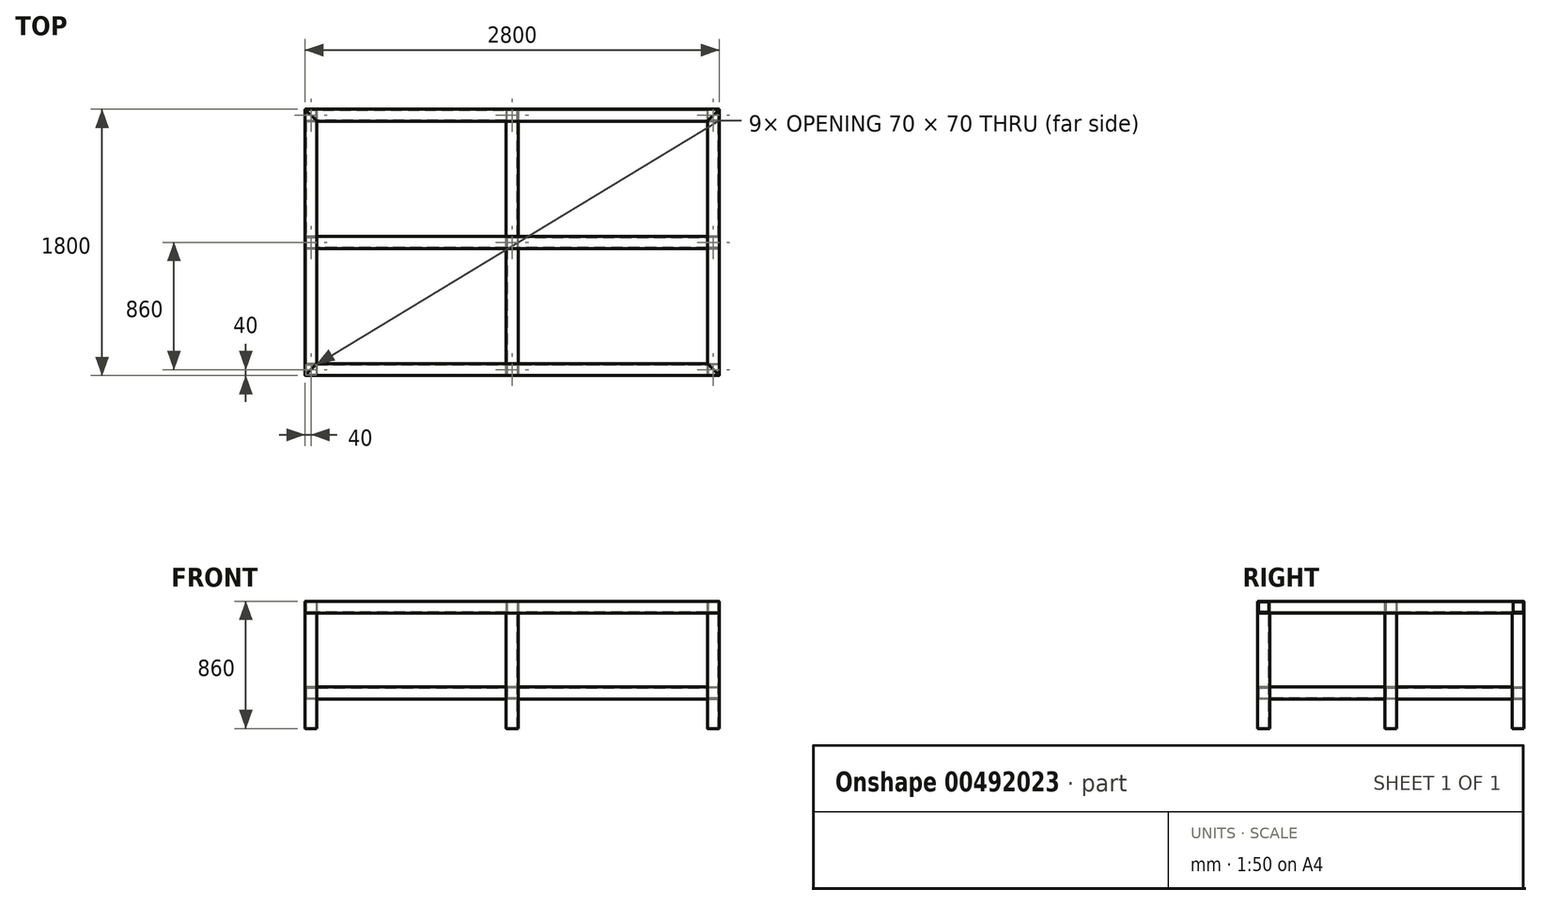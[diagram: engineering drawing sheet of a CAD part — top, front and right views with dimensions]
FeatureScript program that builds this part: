
annotation { "Feature Type Name" : "Feature", "Feature Type Description" : "" }
export const myFeature = defineFeature(function(context is Context, id is Id, definition is map)
    precondition{}
    {
        {
            var Q0;
            Q0=qCreatedBy(makeId("Top.planeOp"),FACE);
            var sketch = newSketch(context, id + "F0", { "sketchPlane" : qUnion([Q0])});
            skLineSegment(sketch, "E0", {"start": v(-1400, -900) * mm, "end": v(-1400, 900) * mm});
            skLineSegment(sketch, "E1", {"start": v(-1400, 900) * mm, "end": v(-1320, 820) * mm});
            skLineSegment(sketch, "E2", {"start": v(-1320, 820) * mm, "end": v(-1320, -820) * mm});
            skLineSegment(sketch, "E3", {"start": v(-1320, -820) * mm, "end": v(-1400, -900) * mm});
            skLineSegment(sketch, "E4.MirrorCS", {"start": v(1320, -820) * mm, "end": v(1400, -900) * mm});
            skLineSegment(sketch, "E5.MirrorCS", {"start": v(1400, 900) * mm, "end": v(1320, 820) * mm});
            skLineSegment(sketch, "E6.MirrorCS", {"start": v(1320, 820) * mm, "end": v(1320, -820) * mm});
            skLineSegment(sketch, "E7.MirrorCS", {"start": v(1400, -900) * mm, "end": v(1400, 900) * mm});
            skSolve(sketch);
        }
        {
            var Q0;
            Q0=makeQuery(id+"F0.imprint","IMPRINT",FACE,{"disambiguationData":[TD([[makeQuery(id+"F0.imprint","IMPRINT",EDGE,{"derivedFrom":sQuery(id+"F0.wireOp",EDGE,"E0")}),-1.0]])]});
            var Q1;
            Q1=makeQuery(id+"F0.imprint","IMPRINT",FACE,{"disambiguationData":[TD([[makeQuery(id+"F0.imprint","IMPRINT",EDGE,{"derivedFrom":sQuery(id+"F0.wireOp",EDGE,"E4.MirrorCS")}),1.0]])]});
            extrude(context, id + "F1", {"entities" : qUnion([Q0, Q1]), "depth" : 80 * mm});
        }
        {
            var Q0;
            Q0=qCreatedBy(makeId("Front.planeOp"),FACE);
            var sketch = newSketch(context, id + "F2", { "sketchPlane" : qUnion([Q0])});
            skLineSegment(sketch, "E8.bottom", {"start": v(-1395, 75) * mm, "end": v(-1325, 75) * mm});
            skLineSegment(sketch, "E8.top", {"start": v(-1395, 5) * mm, "end": v(-1325, 5) * mm});
            skLineSegment(sketch, "E8.left", {"start": v(-1395, 75) * mm, "end": v(-1395, 5) * mm});
            skLineSegment(sketch, "E8.right", {"start": v(-1325, 75) * mm, "end": v(-1325, 5) * mm});
            skLineSegment(sketch, "E9.MirrorCS", {"start": v(1325, 75) * mm, "end": v(1325, 5) * mm});
            skLineSegment(sketch, "E10.MirrorCS", {"start": v(1395, 75) * mm, "end": v(1395, 5) * mm});
            skLineSegment(sketch, "E11.MirrorCS", {"start": v(1395, 75) * mm, "end": v(1325, 75) * mm});
            skLineSegment(sketch, "E12.MirrorCS", {"start": v(1395, 5) * mm, "end": v(1325, 5) * mm});
            skSolve(sketch);
        }
        {
            var Q0;
            Q0 = qSketchRegion(id + "F2", true);
            extrude(context, id + "F3", {"entities" : qUnion([Q0]), "operationType" : NewBodyOperationType.REMOVE, "endBound" : BoundingType.SYMMETRIC, "oppositeDirection" : true, "depth" : 2000 * mm});
        }
        {
            var Q0;
            Q0=makeQuery(id+"F1.opExtrude","CAP_EDGE",EDGE,{"disambiguationData":[OSD([sQuery(id+"F0.wireOp",EDGE,"E0")])],"isStart":false});
            var Q1;
            Q1=makeQuery(id+"F1.opExtrude","CAP_EDGE",EDGE,{"disambiguationData":[OSD([sQuery(id+"F0.wireOp",EDGE,"E2")])],"isStart":false});
            var Q2;
            Q2=makeQuery(id+"F1.opExtrude","CAP_EDGE",EDGE,{"disambiguationData":[OSD([sQuery(id+"F0.wireOp",EDGE,"E2")])],"isStart":true});
            var Q3;
            Q3=makeQuery(id+"F1.opExtrude","CAP_EDGE",EDGE,{"disambiguationData":[OSD([sQuery(id+"F0.wireOp",EDGE,"E0")])],"isStart":true});
            var Q4;
            Q4=makeQuery(id+"F3.boolean.opBoolean","COPY",EDGE,{"derivedFrom":makeQuery(id+"F3.opExtrude","SWEPT_EDGE",EDGE,{"disambiguationData":[OSD([sQuery(id+"F2.wireOp",EDGE,"E8.bottom"),sQuery(id+"F2.wireOp",EDGE,"E8.right")])]})});
            var Q5;
            Q5=makeQuery(id+"F3.boolean.opBoolean","COPY",EDGE,{"derivedFrom":makeQuery(id+"F3.opExtrude","SWEPT_EDGE",EDGE,{"disambiguationData":[OSD([sQuery(id+"F2.wireOp",EDGE,"E8.bottom"),sQuery(id+"F2.wireOp",EDGE,"E8.left")])]})});
            var Q6;
            Q6=makeQuery(id+"F3.boolean.opBoolean","COPY",EDGE,{"derivedFrom":makeQuery(id+"F3.opExtrude","SWEPT_EDGE",EDGE,{"disambiguationData":[OSD([sQuery(id+"F2.wireOp",EDGE,"E8.top"),sQuery(id+"F2.wireOp",EDGE,"E8.right")])]})});
            var Q7;
            Q7=makeQuery(id+"F3.boolean.opBoolean","COPY",EDGE,{"derivedFrom":makeQuery(id+"F3.opExtrude","SWEPT_EDGE",EDGE,{"disambiguationData":[OSD([sQuery(id+"F2.wireOp",EDGE,"E8.top"),sQuery(id+"F2.wireOp",EDGE,"E8.left")])]})});
            fillet(context, id + "F4", {"entities" : qUnion([Q0, Q1, Q2, Q3, Q4, Q5, Q6, Q7]), "radius" : 4 * mm, "tangentPropagation" : true, "allowEdgeOverflow" : false});
        }
        {
            var Q0;
            Q0=makeQuery(id+"F1.opExtrude","CAP_EDGE",EDGE,{"disambiguationData":[OSD([sQuery(id+"F0.wireOp",EDGE,"E7.MirrorCS")])],"isStart":false});
            var Q1;
            Q1=makeQuery(id+"F1.opExtrude","CAP_EDGE",EDGE,{"disambiguationData":[OSD([sQuery(id+"F0.wireOp",EDGE,"E7.MirrorCS")])],"isStart":true});
            var Q2;
            Q2=makeQuery(id+"F1.opExtrude","CAP_EDGE",EDGE,{"disambiguationData":[OSD([sQuery(id+"F0.wireOp",EDGE,"E6.MirrorCS")])],"isStart":false});
            var Q3;
            Q3=makeQuery(id+"F1.opExtrude","CAP_EDGE",EDGE,{"disambiguationData":[OSD([sQuery(id+"F0.wireOp",EDGE,"E6.MirrorCS")])],"isStart":true});
            var Q4;
            Q4=makeQuery(id+"F3.boolean.opBoolean","COPY",EDGE,{"derivedFrom":makeQuery(id+"F3.opExtrude","SWEPT_EDGE",EDGE,{"disambiguationData":[OSD([sQuery(id+"F2.wireOp",EDGE,"E10.MirrorCS"),sQuery(id+"F2.wireOp",EDGE,"E11.MirrorCS")])]})});
            var Q5;
            Q5=makeQuery(id+"F3.boolean.opBoolean","COPY",EDGE,{"derivedFrom":makeQuery(id+"F3.opExtrude","SWEPT_EDGE",EDGE,{"disambiguationData":[OSD([sQuery(id+"F2.wireOp",EDGE,"E10.MirrorCS"),sQuery(id+"F2.wireOp",EDGE,"E12.MirrorCS")])]})});
            var Q6;
            Q6=makeQuery(id+"F3.boolean.opBoolean","COPY",EDGE,{"derivedFrom":makeQuery(id+"F3.opExtrude","SWEPT_EDGE",EDGE,{"disambiguationData":[OSD([sQuery(id+"F2.wireOp",EDGE,"E9.MirrorCS"),sQuery(id+"F2.wireOp",EDGE,"E12.MirrorCS")])]})});
            var Q7;
            Q7=makeQuery(id+"F3.boolean.opBoolean","COPY",EDGE,{"derivedFrom":makeQuery(id+"F3.opExtrude","SWEPT_EDGE",EDGE,{"disambiguationData":[OSD([sQuery(id+"F2.wireOp",EDGE,"E9.MirrorCS"),sQuery(id+"F2.wireOp",EDGE,"E11.MirrorCS")])]})});
            fillet(context, id + "F5", {"entities" : qUnion([Q0, Q1, Q2, Q3, Q4, Q5, Q6, Q7]), "radius" : 4 * mm, "tangentPropagation" : true, "allowEdgeOverflow" : false});
        }
        {
            var Q0;
            Q0=qCreatedBy(makeId("Top.planeOp"),FACE);
            var sketch = newSketch(context, id + "F6", { "sketchPlane" : qUnion([Q0])});
            skLineSegment(sketch, "E13", {"start": v(-1400, 900) * mm, "end": v(1400, 900) * mm});
            skLineSegment(sketch, "E14", {"start": v(1400, 900) * mm, "end": v(1320, 820) * mm});
            skLineSegment(sketch, "E15", {"start": v(1320, 820) * mm, "end": v(-1320, 820) * mm});
            skLineSegment(sketch, "E16", {"start": v(-1320, 820) * mm, "end": v(-1400, 900) * mm});
            skLineSegment(sketch, "E17.MirrorCS", {"start": v(-1320, -820) * mm, "end": v(-1400, -900) * mm});
            skLineSegment(sketch, "E18.MirrorCS", {"start": v(1400, -900) * mm, "end": v(1320, -820) * mm});
            skLineSegment(sketch, "E19.MirrorCS", {"start": v(1320, -820) * mm, "end": v(-1320, -820) * mm});
            skLineSegment(sketch, "E20.MirrorCS", {"start": v(-1400, -900) * mm, "end": v(1400, -900) * mm});
            skSolve(sketch);
        }
        {
            var Q0;
            Q0=makeQuery(id+"F6.imprint","IMPRINT",FACE,{"disambiguationData":[TD([[makeQuery(id+"F6.imprint","IMPRINT",EDGE,{"derivedFrom":sQuery(id+"F6.wireOp",EDGE,"E17.MirrorCS")}),1.0]])]});
            var Q1;
            Q1=makeQuery(id+"F6.imprint","IMPRINT",FACE,{"disambiguationData":[TD([[makeQuery(id+"F6.imprint","IMPRINT",EDGE,{"derivedFrom":sQuery(id+"F6.wireOp",EDGE,"E13")}),-1.0]])]});
            extrude(context, id + "F7", {"entities" : qUnion([Q0, Q1]), "depth" : 80 * mm});
        }
        {
            var Q0;
            Q0=qCreatedBy(makeId("Right.planeOp"),FACE);
            var sketch = newSketch(context, id + "F8", { "sketchPlane" : qUnion([Q0])});
            skLineSegment(sketch, "E21.bottom", {"start": v(-895, 75) * mm, "end": v(-825, 75) * mm});
            skLineSegment(sketch, "E21.top", {"start": v(-895, 5) * mm, "end": v(-825, 5) * mm});
            skLineSegment(sketch, "E21.left", {"start": v(-895, 75) * mm, "end": v(-895, 5) * mm});
            skLineSegment(sketch, "E21.right", {"start": v(-825, 75) * mm, "end": v(-825, 5) * mm});
            skLineSegment(sketch, "E22.MirrorCS", {"start": v(895, 75) * mm, "end": v(895, 5) * mm});
            skLineSegment(sketch, "E23.MirrorCS", {"start": v(895, 75) * mm, "end": v(825, 75) * mm});
            skLineSegment(sketch, "E24.MirrorCS", {"start": v(825, 75) * mm, "end": v(825, 5) * mm});
            skLineSegment(sketch, "E25.MirrorCS", {"start": v(895, 5) * mm, "end": v(825, 5) * mm});
            skSolve(sketch);
        }
        {
            var Q0;
            Q0 = qSketchRegion(id + "F8", true);
            extrude(context, id + "F9", {"entities" : qUnion([Q0]), "operationType" : NewBodyOperationType.REMOVE, "endBound" : BoundingType.SYMMETRIC, "oppositeDirection" : true, "depth" : 2800 * mm});
        }
        {
            var Q0;
            Q0=makeQuery(id+"F7.opExtrude","CAP_EDGE",EDGE,{"disambiguationData":[OSD([sQuery(id+"F6.wireOp",EDGE,"E20.MirrorCS")])],"isStart":true});
            var Q1;
            Q1=makeQuery(id+"F7.opExtrude","CAP_EDGE",EDGE,{"disambiguationData":[OSD([sQuery(id+"F6.wireOp",EDGE,"E19.MirrorCS")])],"isStart":true});
            var Q2;
            Q2=makeQuery(id+"F7.opExtrude","CAP_EDGE",EDGE,{"disambiguationData":[OSD([sQuery(id+"F6.wireOp",EDGE,"E19.MirrorCS")])],"isStart":false});
            var Q3;
            Q3=makeQuery(id+"F7.opExtrude","CAP_EDGE",EDGE,{"disambiguationData":[OSD([sQuery(id+"F6.wireOp",EDGE,"E20.MirrorCS")])],"isStart":false});
            var Q4;
            Q4=makeQuery(id+"F9.boolean.opBoolean","COPY",EDGE,{"derivedFrom":makeQuery(id+"F9.opExtrude","SWEPT_EDGE",EDGE,{"disambiguationData":[OSD([sQuery(id+"F8.wireOp",EDGE,"E21.top"),sQuery(id+"F8.wireOp",EDGE,"E21.left")])]})});
            var Q5;
            Q5=makeQuery(id+"F9.boolean.opBoolean","COPY",EDGE,{"derivedFrom":makeQuery(id+"F9.opExtrude","SWEPT_EDGE",EDGE,{"disambiguationData":[OSD([sQuery(id+"F8.wireOp",EDGE,"E21.top"),sQuery(id+"F8.wireOp",EDGE,"E21.right")])]})});
            var Q6;
            Q6=makeQuery(id+"F9.boolean.opBoolean","COPY",EDGE,{"derivedFrom":makeQuery(id+"F9.opExtrude","SWEPT_EDGE",EDGE,{"disambiguationData":[OSD([sQuery(id+"F8.wireOp",EDGE,"E21.bottom"),sQuery(id+"F8.wireOp",EDGE,"E21.right")])]})});
            var Q7;
            Q7=makeQuery(id+"F9.boolean.opBoolean","COPY",EDGE,{"derivedFrom":makeQuery(id+"F9.opExtrude","SWEPT_EDGE",EDGE,{"disambiguationData":[OSD([sQuery(id+"F8.wireOp",EDGE,"E21.bottom"),sQuery(id+"F8.wireOp",EDGE,"E21.left")])]})});
            fillet(context, id + "F10", {"entities" : qUnion([Q0, Q1, Q2, Q3, Q4, Q5, Q6, Q7]), "radius" : 4 * mm, "tangentPropagation" : true, "allowEdgeOverflow" : false});
        }
        {
            var Q0;
            Q0=makeQuery(id+"F7.opExtrude","CAP_EDGE",EDGE,{"disambiguationData":[OSD([sQuery(id+"F6.wireOp",EDGE,"E15")])],"isStart":false});
            var Q1;
            Q1=makeQuery(id+"F7.opExtrude","CAP_EDGE",EDGE,{"disambiguationData":[OSD([sQuery(id+"F6.wireOp",EDGE,"E13")])],"isStart":false});
            var Q2;
            Q2=makeQuery(id+"F7.opExtrude","CAP_EDGE",EDGE,{"disambiguationData":[OSD([sQuery(id+"F6.wireOp",EDGE,"E15")])],"isStart":true});
            var Q3;
            Q3=makeQuery(id+"F9.boolean.opBoolean","COPY",EDGE,{"derivedFrom":makeQuery(id+"F9.opExtrude","SWEPT_EDGE",EDGE,{"disambiguationData":[OSD([sQuery(id+"F8.wireOp",EDGE,"E22.MirrorCS"),sQuery(id+"F8.wireOp",EDGE,"E25.MirrorCS")])]})});
            var Q4;
            Q4=makeQuery(id+"F9.boolean.opBoolean","COPY",EDGE,{"derivedFrom":makeQuery(id+"F9.opExtrude","SWEPT_EDGE",EDGE,{"disambiguationData":[OSD([sQuery(id+"F8.wireOp",EDGE,"E22.MirrorCS"),sQuery(id+"F8.wireOp",EDGE,"E23.MirrorCS")])]})});
            var Q5;
            Q5=makeQuery(id+"F7.opExtrude","CAP_EDGE",EDGE,{"disambiguationData":[OSD([sQuery(id+"F6.wireOp",EDGE,"E13")])],"isStart":true});
            var Q6;
            Q6=makeQuery(id+"F9.boolean.opBoolean","COPY",EDGE,{"derivedFrom":makeQuery(id+"F9.opExtrude","SWEPT_EDGE",EDGE,{"disambiguationData":[OSD([sQuery(id+"F8.wireOp",EDGE,"E23.MirrorCS"),sQuery(id+"F8.wireOp",EDGE,"E24.MirrorCS")])]})});
            var Q7;
            Q7=makeQuery(id+"F9.boolean.opBoolean","COPY",EDGE,{"derivedFrom":makeQuery(id+"F9.opExtrude","SWEPT_EDGE",EDGE,{"disambiguationData":[OSD([sQuery(id+"F8.wireOp",EDGE,"E24.MirrorCS"),sQuery(id+"F8.wireOp",EDGE,"E25.MirrorCS")])]})});
            fillet(context, id + "F11", {"entities" : qUnion([Q0, Q1, Q2, Q3, Q4, Q5, Q6, Q7]), "radius" : 4 * mm, "tangentPropagation" : true, "allowEdgeOverflow" : false});
        }
        {
            var Q0;
            Q0=qCreatedBy(makeId("Top.planeOp"),FACE);
            var sketch = newSketch(context, id + "F12", { "sketchPlane" : qUnion([Q0])});
            skLineSegment(sketch, "E26.bottom", {"start": v(-1320, 40) * mm, "end": v(1320, 40) * mm});
            skLineSegment(sketch, "E26.top", {"start": v(-1320, -40) * mm, "end": v(1320, -40) * mm});
            skLineSegment(sketch, "E26.left", {"start": v(-1320, 40) * mm, "end": v(-1320, -40) * mm});
            skLineSegment(sketch, "E26.right", {"start": v(1320, 40) * mm, "end": v(1320, -40) * mm});
            skSolve(sketch);
        }
        {
            var Q0;
            Q0=makeQuery(id+"F12.imprint","IMPRINT",FACE,{"disambiguationData":[TD([[makeQuery(id+"F12.imprint","IMPRINT",EDGE,{"derivedFrom":sQuery(id+"F12.wireOp",EDGE,"E26.bottom")}),-1.0]])]});
            extrude(context, id + "F13", {"entities" : qUnion([Q0]), "depth" : 80 * mm});
        }
        {
            var Q0;
            Q0=makeQuery(id+"F13.opExtrude","SWEPT_FACE",FACE,{"disambiguationData":[OSD([sQuery(id+"F12.wireOp",EDGE,"E26.left")])]});
            var sketch = newSketch(context, id + "F14", { "sketchPlane" : qUnion([Q0])});
            skLineSegment(sketch, "E27.bottom", {"start": v(-35, 5) * mm, "end": v(35, 5) * mm});
            skLineSegment(sketch, "E27.top", {"start": v(-35, 75) * mm, "end": v(35, 75) * mm});
            skLineSegment(sketch, "E27.left", {"start": v(-35, 5) * mm, "end": v(-35, 75) * mm});
            skLineSegment(sketch, "E27.right", {"start": v(35, 5) * mm, "end": v(35, 75) * mm});
            skSolve(sketch);
        }
        {
            var Q0;
            Q0 = qSketchRegion(id + "F14", true);
            extrude(context, id + "F15", {"entities" : qUnion([Q0]), "operationType" : NewBodyOperationType.REMOVE, "oppositeDirection" : true, "depth" : 2640 * mm});
        }
        {
            var Q0;
            Q0=makeQuery(id+"F13.opExtrude","CAP_EDGE",EDGE,{"disambiguationData":[OSD([sQuery(id+"F12.wireOp",EDGE,"E26.top")])],"isStart":true});
            var Q1;
            Q1=makeQuery(id+"F13.opExtrude","CAP_EDGE",EDGE,{"disambiguationData":[OSD([sQuery(id+"F12.wireOp",EDGE,"E26.bottom")])],"isStart":true});
            var Q2;
            Q2=makeQuery(id+"F13.opExtrude","CAP_EDGE",EDGE,{"disambiguationData":[OSD([sQuery(id+"F12.wireOp",EDGE,"E26.bottom")])],"isStart":false});
            var Q3;
            Q3=makeQuery(id+"F15.boolean.opBoolean","COPY",EDGE,{"derivedFrom":makeQuery(id+"F15.opExtrude","SWEPT_EDGE",EDGE,{"disambiguationData":[OSD([sQuery(id+"F14.wireOp",EDGE,"E27.top"),sQuery(id+"F14.wireOp",EDGE,"E27.right")])]})});
            var Q4;
            Q4=makeQuery(id+"F13.opExtrude","CAP_EDGE",EDGE,{"disambiguationData":[OSD([sQuery(id+"F12.wireOp",EDGE,"E26.top")])],"isStart":false});
            var Q5;
            Q5=makeQuery(id+"F15.boolean.opBoolean","COPY",EDGE,{"derivedFrom":makeQuery(id+"F15.opExtrude","SWEPT_EDGE",EDGE,{"disambiguationData":[OSD([sQuery(id+"F14.wireOp",EDGE,"E27.bottom"),sQuery(id+"F14.wireOp",EDGE,"E27.right")])]})});
            var Q6;
            Q6=makeQuery(id+"F15.boolean.opBoolean","COPY",EDGE,{"derivedFrom":makeQuery(id+"F15.opExtrude","SWEPT_EDGE",EDGE,{"disambiguationData":[OSD([sQuery(id+"F14.wireOp",EDGE,"E27.bottom"),sQuery(id+"F14.wireOp",EDGE,"E27.left")])]})});
            var Q7;
            Q7=makeQuery(id+"F15.boolean.opBoolean","COPY",EDGE,{"derivedFrom":makeQuery(id+"F15.opExtrude","SWEPT_EDGE",EDGE,{"disambiguationData":[OSD([sQuery(id+"F14.wireOp",EDGE,"E27.top"),sQuery(id+"F14.wireOp",EDGE,"E27.left")])]})});
            fillet(context, id + "F16", {"entities" : qUnion([Q0, Q1, Q2, Q3, Q4, Q5, Q6, Q7]), "radius" : 5 * mm, "tangentPropagation" : true, "allowEdgeOverflow" : false});
        }
        {
            var Q0;
            Q0=qCreatedBy(makeId("Top.planeOp"),FACE);
            var sketch = newSketch(context, id + "F17", { "sketchPlane" : qUnion([Q0])});
            skLineSegment(sketch, "E28.bottom", {"start": v(-40, 820) * mm, "end": v(40, 820) * mm});
            skLineSegment(sketch, "E28.top", {"start": v(-40, 40) * mm, "end": v(40, 40) * mm});
            skLineSegment(sketch, "E28.left", {"start": v(-40, 820) * mm, "end": v(-40, 40) * mm});
            skLineSegment(sketch, "E28.right", {"start": v(40, 820) * mm, "end": v(40, 40) * mm});
            skLineSegment(sketch, "E29.bottom", {"start": v(-40, -40) * mm, "end": v(40, -40) * mm});
            skLineSegment(sketch, "E29.top", {"start": v(-40, -820) * mm, "end": v(40, -820) * mm});
            skLineSegment(sketch, "E29.left", {"start": v(-40, -40) * mm, "end": v(-40, -820) * mm});
            skLineSegment(sketch, "E29.right", {"start": v(40, -40) * mm, "end": v(40, -820) * mm});
            skSolve(sketch);
        }
        {
            var Q0;
            Q0 = qSketchRegion(id + "F17", true);
            extrude(context, id + "F18", {"entities" : qUnion([Q0]), "depth" : 80 * mm});
        }
        {
            var Q0;
            Q0=makeQuery(id+"F18.opExtrude","SWEPT_FACE",FACE,{"disambiguationData":[OSD([sQuery(id+"F17.wireOp",EDGE,"E29.top")])]});
            var sketch = newSketch(context, id + "F19", { "sketchPlane" : qUnion([Q0])});
            skLineSegment(sketch, "E30.bottom", {"start": v(-35, 75) * mm, "end": v(35, 75) * mm});
            skLineSegment(sketch, "E30.top", {"start": v(-35, 5) * mm, "end": v(35, 5) * mm});
            skLineSegment(sketch, "E30.left", {"start": v(-35, 75) * mm, "end": v(-35, 5) * mm});
            skLineSegment(sketch, "E30.right", {"start": v(35, 75) * mm, "end": v(35, 5) * mm});
            skSolve(sketch);
        }
        {
            var Q0;
            Q0 = qSketchRegion(id + "F19", true);
            extrude(context, id + "F20", {"entities" : qUnion([Q0]), "operationType" : NewBodyOperationType.REMOVE, "oppositeDirection" : true, "depth" : 1560 * mm});
        }
        {
            var Q0;
            Q0=makeQuery(id+"F18.opExtrude","SWEPT_FACE",FACE,{"disambiguationData":[OSD([sQuery(id+"F17.wireOp",EDGE,"E28.bottom")])]});
            var sketch = newSketch(context, id + "F21", { "sketchPlane" : qUnion([Q0])});
            skLineSegment(sketch, "E31.bottom", {"start": v(35, 75) * mm, "end": v(-35, 75) * mm});
            skLineSegment(sketch, "E31.top", {"start": v(35, 5) * mm, "end": v(-35, 5) * mm});
            skLineSegment(sketch, "E31.left", {"start": v(35, 75) * mm, "end": v(35, 5) * mm});
            skLineSegment(sketch, "E31.right", {"start": v(-35, 75) * mm, "end": v(-35, 5) * mm});
            skSolve(sketch);
        }
        {
            var Q0;
            Q0 = qSketchRegion(id + "F21", true);
            extrude(context, id + "F22", {"entities" : qUnion([Q0]), "operationType" : NewBodyOperationType.REMOVE, "oppositeDirection" : true, "depth" : 1640 * mm});
        }
        {
            var Q0;
            Q0=makeQuery(id+"F18.opExtrude","CAP_EDGE",EDGE,{"disambiguationData":[OSD([sQuery(id+"F17.wireOp",EDGE,"E28.right")])],"isStart":false});
            var Q1;
            Q1=makeQuery(id+"F18.opExtrude","CAP_EDGE",EDGE,{"disambiguationData":[OSD([sQuery(id+"F17.wireOp",EDGE,"E28.left")])],"isStart":false});
            var Q2;
            Q2=makeQuery(id+"F18.opExtrude","CAP_EDGE",EDGE,{"disambiguationData":[OSD([sQuery(id+"F17.wireOp",EDGE,"E28.right")])],"isStart":true});
            var Q3;
            Q3=makeQuery(id+"F18.opExtrude","CAP_EDGE",EDGE,{"disambiguationData":[OSD([sQuery(id+"F17.wireOp",EDGE,"E28.left")])],"isStart":true});
            var Q4;
            Q4=makeQuery(id+"F22.boolean.opBoolean","COPY",EDGE,{"derivedFrom":makeQuery(id+"F22.opExtrude","SWEPT_EDGE",EDGE,{"disambiguationData":[OSD([sQuery(id+"F21.wireOp",EDGE,"E31.bottom"),sQuery(id+"F21.wireOp",EDGE,"E31.right")])]})});
            var Q5;
            Q5=makeQuery(id+"F22.boolean.opBoolean","COPY",EDGE,{"derivedFrom":makeQuery(id+"F22.opExtrude","SWEPT_EDGE",EDGE,{"disambiguationData":[OSD([sQuery(id+"F21.wireOp",EDGE,"E31.top"),sQuery(id+"F21.wireOp",EDGE,"E31.right")])]})});
            var Q6;
            Q6=makeQuery(id+"F22.boolean.opBoolean","COPY",EDGE,{"derivedFrom":makeQuery(id+"F22.opExtrude","SWEPT_EDGE",EDGE,{"disambiguationData":[OSD([sQuery(id+"F21.wireOp",EDGE,"E31.top"),sQuery(id+"F21.wireOp",EDGE,"E31.left")])]})});
            var Q7;
            Q7=makeQuery(id+"F22.boolean.opBoolean","COPY",EDGE,{"derivedFrom":makeQuery(id+"F22.opExtrude","SWEPT_EDGE",EDGE,{"disambiguationData":[OSD([sQuery(id+"F21.wireOp",EDGE,"E31.bottom"),sQuery(id+"F21.wireOp",EDGE,"E31.left")])]})});
            fillet(context, id + "F23", {"entities" : qUnion([Q0, Q1, Q2, Q3, Q4, Q5, Q6, Q7]), "radius" : 5 * mm, "tangentPropagation" : true, "allowEdgeOverflow" : false});
        }
        {
            var Q0;
            Q0=makeQuery(id+"F7.opExtrude","CAP_FACE",FACE,{"disambiguationData":[OSD([sQuery(id+"F6.wireOp",EDGE,"E17.MirrorCS"),sQuery(id+"F6.wireOp",EDGE,"E18.MirrorCS"),sQuery(id+"F6.wireOp",EDGE,"E19.MirrorCS"),sQuery(id+"F6.wireOp",EDGE,"E20.MirrorCS")])],"isStart":false});
            var sketch = newSketch(context, id + "F24", { "sketchPlane" : qUnion([Q0])});
            skLineSegment(sketch, "E32.bottom", {"start": v(1500, -1000) * mm, "end": v(-1500, -1000) * mm});
            skLineSegment(sketch, "E32.top", {"start": v(1500, 1000) * mm, "end": v(-1500, 1000) * mm});
            skLineSegment(sketch, "E32.left", {"start": v(1500, -1000) * mm, "end": v(1500, 1000) * mm});
            skLineSegment(sketch, "E32.right", {"start": v(-1500, -1000) * mm, "end": v(-1500, 1000) * mm});
            skSolve(sketch);
        }
        {
            var Q0;
            Q0 = qSketchRegion(id + "F24", true);
            extrude(context, id + "F25", {"entities" : qUnion([Q0]), "depth" : 60 * mm});
        }
        {
            var Q0;
            Q0=makeQuery(id+"F1.opExtrude","CAP_FACE",FACE,{"disambiguationData":[OSD([sQuery(id+"F0.wireOp",EDGE,"E4.MirrorCS"),sQuery(id+"F0.wireOp",EDGE,"E5.MirrorCS"),sQuery(id+"F0.wireOp",EDGE,"E6.MirrorCS"),sQuery(id+"F0.wireOp",EDGE,"E7.MirrorCS")])],"isStart":true});
            var sketch = newSketch(context, id + "F26", { "sketchPlane" : qUnion([Q0])});
            skLineSegment(sketch, "E33.bottom", {"start": v(1396, -900) * mm, "end": v(1324, -900) * mm});
            skLineSegment(sketch, "E33.top", {"start": v(1396, -820) * mm, "end": v(1324, -820) * mm});
            skLineSegment(sketch, "E33.left", {"start": v(1400, -896) * mm, "end": v(1400, -824) * mm});
            skLineSegment(sketch, "E33.right", {"start": v(1320, -896) * mm, "end": v(1320, -824) * mm});
            skLineSegment(sketch, "E34.bottom", {"start": v(1391, -825) * mm, "end": v(1329, -825) * mm});
            skLineSegment(sketch, "E34.top", {"start": v(1391, -895) * mm, "end": v(1329, -895) * mm});
            skLineSegment(sketch, "E34.left", {"start": v(1395, -829) * mm, "end": v(1395, -891) * mm});
            skLineSegment(sketch, "E34.right", {"start": v(1325, -829) * mm, "end": v(1325, -891) * mm});
            skPoint(sketch, "E35.visualSharp", {"position": v(1400, -820) * mm});
            skArc(sketch, "E35.filletArc", {"start": v(1400, -824) * mm, "mid": v(1398.83, -821.17) * mm, "end": v(1396, -820) * mm});
            skPoint(sketch, "E36.visualSharp", {"position": v(1395, -825) * mm});
            skArc(sketch, "E36.filletArc", {"start": v(1395, -829) * mm, "mid": v(1393.83, -826.17) * mm, "end": v(1391, -825) * mm});
            skPoint(sketch, "E37.visualSharp", {"position": v(1400, -900) * mm});
            skArc(sketch, "E37.filletArc", {"start": v(1396, -900) * mm, "mid": v(1398.83, -898.83) * mm, "end": v(1400, -896) * mm});
            skPoint(sketch, "E38.visualSharp", {"position": v(1395, -895) * mm});
            skArc(sketch, "E38.filletArc", {"start": v(1391, -895) * mm, "mid": v(1393.83, -893.83) * mm, "end": v(1395, -891) * mm});
            skPoint(sketch, "E39.visualSharp", {"position": v(1325, -895) * mm});
            skArc(sketch, "E39.filletArc", {"start": v(1325, -891) * mm, "mid": v(1326.17, -893.83) * mm, "end": v(1329, -895) * mm});
            skPoint(sketch, "E40.visualSharp", {"position": v(1325, -825) * mm});
            skArc(sketch, "E40.filletArc", {"start": v(1329, -825) * mm, "mid": v(1326.17, -826.17) * mm, "end": v(1325, -829) * mm});
            skPoint(sketch, "E41.visualSharp", {"position": v(1320, -820) * mm});
            skArc(sketch, "E41.filletArc", {"start": v(1324, -820) * mm, "mid": v(1321.17, -821.17) * mm, "end": v(1320, -824) * mm});
            skPoint(sketch, "E42.visualSharp", {"position": v(1320, -900) * mm});
            skArc(sketch, "E42.filletArc", {"start": v(1320, -896) * mm, "mid": v(1321.17, -898.83) * mm, "end": v(1324, -900) * mm});
            skLineSegment(sketch, "E43", {"start": v(0, 0) * mm, "end": v(0, -1044.98) * mm, "construction": true});
            skLineSegment(sketch, "E44", {"start": v(0, 0) * mm, "end": v(1566.73, 0) * mm, "construction": true});
            skPoint(sketch, "E44.endSnap0", {"position": v(1396, 0) * mm});
            skArc(sketch, "E45.MirrorCS", {"start": v(1391, 895) * mm, "mid": v(1393.83, 893.83) * mm, "end": v(1395, 891) * mm});
            skArc(sketch, "E46.MirrorCS", {"start": v(1325, 891) * mm, "mid": v(1326.17, 893.83) * mm, "end": v(1329, 895) * mm});
            skArc(sketch, "E47.MirrorCS", {"start": v(1324, 820) * mm, "mid": v(1321.17, 821.17) * mm, "end": v(1320, 824) * mm});
            skArc(sketch, "E48.MirrorCS", {"start": v(1320, 896) * mm, "mid": v(1321.17, 898.83) * mm, "end": v(1324, 900) * mm});
            skLineSegment(sketch, "E49.MirrorCS", {"start": v(1391, 895) * mm, "end": v(1329, 895) * mm});
            skLineSegment(sketch, "E50.MirrorCS", {"start": v(1396, 900) * mm, "end": v(1324, 900) * mm});
            skArc(sketch, "E51.MirrorCS", {"start": v(1396, 900) * mm, "mid": v(1398.83, 898.83) * mm, "end": v(1400, 896) * mm});
            skArc(sketch, "E52.MirrorCS", {"start": v(1329, 825) * mm, "mid": v(1326.17, 826.17) * mm, "end": v(1325, 829) * mm});
            skArc(sketch, "E53.MirrorCS", {"start": v(1400, 824) * mm, "mid": v(1398.83, 821.17) * mm, "end": v(1396, 820) * mm});
            skLineSegment(sketch, "E54.MirrorCS", {"start": v(1395, 829) * mm, "end": v(1395, 891) * mm});
            skLineSegment(sketch, "E55.MirrorCS", {"start": v(1396, 820) * mm, "end": v(1324, 820) * mm});
            skLineSegment(sketch, "E56.MirrorCS", {"start": v(1320, 896) * mm, "end": v(1320, 824) * mm});
            skArc(sketch, "E57.MirrorCS", {"start": v(1395, 829) * mm, "mid": v(1393.83, 826.17) * mm, "end": v(1391, 825) * mm});
            skLineSegment(sketch, "E58.MirrorCS", {"start": v(1391, 825) * mm, "end": v(1329, 825) * mm});
            skLineSegment(sketch, "E59.MirrorCS", {"start": v(1400, 896) * mm, "end": v(1400, 824) * mm});
            skLineSegment(sketch, "E60.MirrorCS", {"start": v(1325, 829) * mm, "end": v(1325, 891) * mm});
            skPoint(sketch, "E61.MirrorP", {"position": v(1325, 895) * mm});
            skPoint(sketch, "E62.MirrorP", {"position": v(1325, 825) * mm});
            skPoint(sketch, "E63.MirrorP", {"position": v(1395, 895) * mm});
            skPoint(sketch, "E64.MirrorP", {"position": v(1400, 900) * mm});
            skPoint(sketch, "E65.MirrorP", {"position": v(1400, 820) * mm});
            skPoint(sketch, "E66.MirrorP", {"position": v(1320, 820) * mm});
            skPoint(sketch, "E67.MirrorP", {"position": v(1320, 900) * mm});
            skPoint(sketch, "E68.MirrorP", {"position": v(1395, 825) * mm});
            skArc(sketch, "E69.MirrorCS", {"start": v(-1329, 825) * mm, "mid": v(-1326.17, 826.17) * mm, "end": v(-1325, 829) * mm});
            skLineSegment(sketch, "E70.MirrorCS", {"start": v(-1400, 896) * mm, "end": v(-1400, 824) * mm});
            skArc(sketch, "E71.MirrorCS", {"start": v(-1396, 900) * mm, "mid": v(-1398.83, 898.83) * mm, "end": v(-1400, 896) * mm});
            skLineSegment(sketch, "E72.MirrorCS", {"start": v(-1320, 896) * mm, "end": v(-1320, 824) * mm});
            skArc(sketch, "E73.MirrorCS", {"start": v(-1324, 820) * mm, "mid": v(-1321.17, 821.17) * mm, "end": v(-1320, 824) * mm});
            skArc(sketch, "E74.MirrorCS", {"start": v(-1325, 891) * mm, "mid": v(-1326.17, 893.83) * mm, "end": v(-1329, 895) * mm});
            skArc(sketch, "E75.MirrorCS", {"start": v(-1400, 824) * mm, "mid": v(-1398.83, 821.17) * mm, "end": v(-1396, 820) * mm});
            skArc(sketch, "E76.MirrorCS", {"start": v(-1391, 895) * mm, "mid": v(-1393.83, 893.83) * mm, "end": v(-1395, 891) * mm});
            skArc(sketch, "E77.MirrorCS", {"start": v(-1395, 829) * mm, "mid": v(-1393.83, 826.17) * mm, "end": v(-1391, 825) * mm});
            skArc(sketch, "E78.MirrorCS", {"start": v(-1320, 896) * mm, "mid": v(-1321.17, 898.83) * mm, "end": v(-1324, 900) * mm});
            skLineSegment(sketch, "E79.MirrorCS", {"start": v(-1391, 895) * mm, "end": v(-1329, 895) * mm});
            skLineSegment(sketch, "E80.MirrorCS", {"start": v(-1395, 829) * mm, "end": v(-1395, 891) * mm});
            skLineSegment(sketch, "E81.MirrorCS", {"start": v(-1396, 820) * mm, "end": v(-1324, 820) * mm});
            skLineSegment(sketch, "E82.MirrorCS", {"start": v(-1325, 829) * mm, "end": v(-1325, 891) * mm});
            skLineSegment(sketch, "E83.MirrorCS", {"start": v(-1391, 825) * mm, "end": v(-1329, 825) * mm});
            skLineSegment(sketch, "E84.MirrorCS", {"start": v(-1396, 900) * mm, "end": v(-1324, 900) * mm});
            skPoint(sketch, "E85.MirrorP", {"position": v(-1395, 895) * mm});
            skPoint(sketch, "E86.MirrorP", {"position": v(-1400, 820) * mm});
            skPoint(sketch, "E87.MirrorP", {"position": v(-1325, 825) * mm});
            skPoint(sketch, "E88.MirrorP", {"position": v(-1400, 900) * mm});
            skPoint(sketch, "E89.MirrorP", {"position": v(-1395, 825) * mm});
            skPoint(sketch, "E90.MirrorP", {"position": v(-1325, 895) * mm});
            skPoint(sketch, "E91.MirrorP", {"position": v(-1320, 900) * mm});
            skPoint(sketch, "E92.MirrorP", {"position": v(-1320, 820) * mm});
            skArc(sketch, "E93.MirrorCS", {"start": v(-1329, -825) * mm, "mid": v(-1326.17, -826.17) * mm, "end": v(-1325, -829) * mm});
            skArc(sketch, "E94.MirrorCS", {"start": v(-1324, -820) * mm, "mid": v(-1321.17, -821.17) * mm, "end": v(-1320, -824) * mm});
            skArc(sketch, "E95.MirrorCS", {"start": v(-1396, -900) * mm, "mid": v(-1398.83, -898.83) * mm, "end": v(-1400, -896) * mm});
            skArc(sketch, "E96.MirrorCS", {"start": v(-1400, -824) * mm, "mid": v(-1398.83, -821.17) * mm, "end": v(-1396, -820) * mm});
            skLineSegment(sketch, "E97.MirrorCS", {"start": v(-1400, -896) * mm, "end": v(-1400, -824) * mm});
            skLineSegment(sketch, "E98.MirrorCS", {"start": v(-1396, -820) * mm, "end": v(-1324, -820) * mm});
            skArc(sketch, "E99.MirrorCS", {"start": v(-1320, -896) * mm, "mid": v(-1321.17, -898.83) * mm, "end": v(-1324, -900) * mm});
            skArc(sketch, "E100.MirrorCS", {"start": v(-1325, -891) * mm, "mid": v(-1326.17, -893.83) * mm, "end": v(-1329, -895) * mm});
            skArc(sketch, "E101.MirrorCS", {"start": v(-1391, -895) * mm, "mid": v(-1393.83, -893.83) * mm, "end": v(-1395, -891) * mm});
            skArc(sketch, "E102.MirrorCS", {"start": v(-1395, -829) * mm, "mid": v(-1393.83, -826.17) * mm, "end": v(-1391, -825) * mm});
            skLineSegment(sketch, "E103.MirrorCS", {"start": v(-1395, -829) * mm, "end": v(-1395, -891) * mm});
            skLineSegment(sketch, "E104.MirrorCS", {"start": v(-1391, -895) * mm, "end": v(-1329, -895) * mm});
            skLineSegment(sketch, "E105.MirrorCS", {"start": v(-1391, -825) * mm, "end": v(-1329, -825) * mm});
            skLineSegment(sketch, "E106.MirrorCS", {"start": v(-1320, -896) * mm, "end": v(-1320, -824) * mm});
            skLineSegment(sketch, "E107.MirrorCS", {"start": v(-1325, -829) * mm, "end": v(-1325, -891) * mm});
            skLineSegment(sketch, "E108.MirrorCS", {"start": v(-1396, -900) * mm, "end": v(-1324, -900) * mm});
            skPoint(sketch, "E109.MirrorP", {"position": v(-1395, -825) * mm});
            skPoint(sketch, "E110.MirrorP", {"position": v(-1325, -895) * mm});
            skPoint(sketch, "E111.MirrorP", {"position": v(-1325, -825) * mm});
            skPoint(sketch, "E112.MirrorP", {"position": v(-1400, -900) * mm});
            skPoint(sketch, "E113.MirrorP", {"position": v(-1320, -820) * mm});
            skPoint(sketch, "E114.MirrorP", {"position": v(-1400, -820) * mm});
            skPoint(sketch, "E115.MirrorP", {"position": v(-1395, -895) * mm});
            skPoint(sketch, "E116.MirrorP", {"position": v(-1320, -900) * mm});
            skLineSegment(sketch, "E117", {"start": v(1360, -306.61) * mm, "end": v(1360, -707.73) * mm, "construction": true});
            skPoint(sketch, "E117.startSnap0", {"position": v(1360, -895) * mm});
            skLineSegment(sketch, "E118", {"start": v(1360, -306.61) * mm, "end": v(0, -306.61) * mm, "construction": true});
            skLineSegment(sketch, "E119", {"start": v(680, -306.61) * mm, "end": v(680, -680.68) * mm, "construction": true});
            skArc(sketch, "E120.MirrorCS", {"start": v(31, -825) * mm, "mid": v(33.83, -826.17) * mm, "end": v(35, -829) * mm});
            skArc(sketch, "E121.MirrorCS", {"start": v(36, -820) * mm, "mid": v(38.83, -821.17) * mm, "end": v(40, -824) * mm});
            skArc(sketch, "E122.MirrorCS", {"start": v(40, -896) * mm, "mid": v(38.83, -898.83) * mm, "end": v(36, -900) * mm});
            skLineSegment(sketch, "E123.MirrorCS", {"start": v(-36, -900) * mm, "end": v(36, -900) * mm});
            skLineSegment(sketch, "E124.MirrorCS", {"start": v(-36, -820) * mm, "end": v(36, -820) * mm});
            skLineSegment(sketch, "E125.MirrorCS", {"start": v(-40, -896) * mm, "end": v(-40, -824) * mm});
            skLineSegment(sketch, "E126.MirrorCS", {"start": v(40, -896) * mm, "end": v(40, -824) * mm});
            skLineSegment(sketch, "E127.MirrorCS", {"start": v(-31, -825) * mm, "end": v(31, -825) * mm});
            skLineSegment(sketch, "E128.MirrorCS", {"start": v(-31, -895) * mm, "end": v(31, -895) * mm});
            skLineSegment(sketch, "E129.MirrorCS", {"start": v(-35, -829) * mm, "end": v(-35, -891) * mm});
            skLineSegment(sketch, "E130.MirrorCS", {"start": v(35, -829) * mm, "end": v(35, -891) * mm});
            skArc(sketch, "E131.MirrorCS", {"start": v(-40, -824) * mm, "mid": v(-38.83, -821.17) * mm, "end": v(-36, -820) * mm});
            skArc(sketch, "E132.MirrorCS", {"start": v(-35, -829) * mm, "mid": v(-33.83, -826.17) * mm, "end": v(-31, -825) * mm});
            skArc(sketch, "E133.MirrorCS", {"start": v(-36, -900) * mm, "mid": v(-38.83, -898.83) * mm, "end": v(-40, -896) * mm});
            skArc(sketch, "E134.MirrorCS", {"start": v(-31, -895) * mm, "mid": v(-33.83, -893.83) * mm, "end": v(-35, -891) * mm});
            skArc(sketch, "E135.MirrorCS", {"start": v(35, -891) * mm, "mid": v(33.83, -893.83) * mm, "end": v(31, -895) * mm});
            skPoint(sketch, "E136.MirrorP", {"position": v(0, -895) * mm});
            skPoint(sketch, "E137.MirrorP", {"position": v(-40, -900) * mm});
            skPoint(sketch, "E138.MirrorP", {"position": v(-35, -825) * mm});
            skPoint(sketch, "E139.MirrorP", {"position": v(35, -825) * mm});
            skPoint(sketch, "E140.MirrorP", {"position": v(35, -895) * mm});
            skPoint(sketch, "E141.MirrorP", {"position": v(-35, -895) * mm});
            skPoint(sketch, "E142.MirrorP", {"position": v(40, -820) * mm});
            skPoint(sketch, "E143.MirrorP", {"position": v(-40, -820) * mm});
            skPoint(sketch, "E144.MirrorP", {"position": v(40, -900) * mm});
            skArc(sketch, "E145.MirrorCS", {"start": v(-35, -891) * mm, "mid": v(-33.83, -893.83) * mm, "end": v(-31, -895) * mm});
            skLineSegment(sketch, "E146.MirrorCS", {"start": v(31, -895) * mm, "end": v(-31, -895) * mm});
            skArc(sketch, "E147.MirrorCS", {"start": v(35, -829) * mm, "mid": v(33.83, -826.17) * mm, "end": v(31, -825) * mm});
            skLineSegment(sketch, "E148.MirrorCS", {"start": v(36, -900) * mm, "end": v(-36, -900) * mm});
            skArc(sketch, "E149.MirrorCS", {"start": v(-40, -896) * mm, "mid": v(-38.83, -898.83) * mm, "end": v(-36, -900) * mm});
            skArc(sketch, "E150.MirrorCS", {"start": v(-31, -825) * mm, "mid": v(-33.83, -826.17) * mm, "end": v(-35, -829) * mm});
            skArc(sketch, "E151.MirrorCS", {"start": v(31, -895) * mm, "mid": v(33.83, -893.83) * mm, "end": v(35, -891) * mm});
            skArc(sketch, "E152.MirrorCS", {"start": v(36, -900) * mm, "mid": v(38.83, -898.83) * mm, "end": v(40, -896) * mm});
            skArc(sketch, "E153.MirrorCS", {"start": v(40, -824) * mm, "mid": v(38.83, -821.17) * mm, "end": v(36, -820) * mm});
            skArc(sketch, "E154.MirrorCS", {"start": v(-36, -820) * mm, "mid": v(-38.83, -821.17) * mm, "end": v(-40, -824) * mm});
            skLineSegment(sketch, "E155.MirrorCS", {"start": v(36, -820) * mm, "end": v(-36, -820) * mm});
            skLineSegment(sketch, "E156.MirrorCS", {"start": v(31, -825) * mm, "end": v(-31, -825) * mm});
            skLineSegment(sketch, "E157.MirrorCS", {"start": v(0, 0) * mm, "end": v(-1566.73, 0) * mm, "construction": true});
            skLineSegment(sketch, "E158", {"start": v(1169.83, -860) * mm, "end": v(841.5, -860) * mm, "construction": true});
            skLineSegment(sketch, "E159", {"start": v(1005.66, -860) * mm, "end": v(1005.66, 0) * mm, "construction": true});
            skLineSegment(sketch, "E160", {"start": v(1005.66, -430) * mm, "end": v(848.86, -430) * mm, "construction": true});
            skArc(sketch, "E161.MirrorCS", {"start": v(36, 40) * mm, "mid": v(38.83, 38.83) * mm, "end": v(40, 36) * mm});
            skArc(sketch, "E162.MirrorCS", {"start": v(31, 35) * mm, "mid": v(33.83, 33.83) * mm, "end": v(35, 31) * mm});
            skArc(sketch, "E163.MirrorCS", {"start": v(40, 36) * mm, "mid": v(38.83, 38.83) * mm, "end": v(36, 40) * mm});
            skArc(sketch, "E164.MirrorCS", {"start": v(35, 31) * mm, "mid": v(33.83, 33.83) * mm, "end": v(31, 35) * mm});
            skLineSegment(sketch, "E165.MirrorCS", {"start": v(35, -31) * mm, "end": v(35, 31) * mm});
            skLineSegment(sketch, "E166.MirrorCS", {"start": v(40, 36) * mm, "end": v(40, -36) * mm});
            skArc(sketch, "E167.MirrorCS", {"start": v(40, -36) * mm, "mid": v(38.83, -38.83) * mm, "end": v(36, -40) * mm});
            skArc(sketch, "E168.MirrorCS", {"start": v(36, -40) * mm, "mid": v(38.83, -38.83) * mm, "end": v(40, -36) * mm});
            skArc(sketch, "E169.MirrorCS", {"start": v(31, -35) * mm, "mid": v(33.83, -33.83) * mm, "end": v(35, -31) * mm});
            skArc(sketch, "E170.MirrorCS", {"start": v(-35, 31) * mm, "mid": v(-33.83, 33.83) * mm, "end": v(-31, 35) * mm});
            skArc(sketch, "E171.MirrorCS", {"start": v(-31, -35) * mm, "mid": v(-33.83, -33.83) * mm, "end": v(-35, -31) * mm});
            skLineSegment(sketch, "E172.MirrorCS", {"start": v(-36, 40) * mm, "end": v(36, 40) * mm});
            skArc(sketch, "E173.MirrorCS", {"start": v(-36, 40) * mm, "mid": v(-38.83, 38.83) * mm, "end": v(-40, 36) * mm});
            skLineSegment(sketch, "E174.MirrorCS", {"start": v(-31, 35) * mm, "end": v(31, 35) * mm});
            skArc(sketch, "E175.MirrorCS", {"start": v(-36, -40) * mm, "mid": v(-38.83, -38.83) * mm, "end": v(-40, -36) * mm});
            skLineSegment(sketch, "E176.MirrorCS", {"start": v(36, 40) * mm, "end": v(-36, 40) * mm});
            skArc(sketch, "E177.MirrorCS", {"start": v(-40, -36) * mm, "mid": v(-38.83, -38.83) * mm, "end": v(-36, -40) * mm});
            skArc(sketch, "E178.MirrorCS", {"start": v(35, -31) * mm, "mid": v(33.83, -33.83) * mm, "end": v(31, -35) * mm});
            skArc(sketch, "E179.MirrorCS", {"start": v(-40, 36) * mm, "mid": v(-38.83, 38.83) * mm, "end": v(-36, 40) * mm});
            skArc(sketch, "E180.MirrorCS", {"start": v(-31, 35) * mm, "mid": v(-33.83, 33.83) * mm, "end": v(-35, 31) * mm});
            skArc(sketch, "E181.MirrorCS", {"start": v(-35, -31) * mm, "mid": v(-33.83, -33.83) * mm, "end": v(-31, -35) * mm});
            skLineSegment(sketch, "E182.MirrorCS", {"start": v(-31, -35) * mm, "end": v(31, -35) * mm});
            skLineSegment(sketch, "E183.MirrorCS", {"start": v(31, 35) * mm, "end": v(-31, 35) * mm});
            skLineSegment(sketch, "E184.MirrorCS", {"start": v(-36, -40) * mm, "end": v(36, -40) * mm});
            skLineSegment(sketch, "E185.MirrorCS", {"start": v(31, -35) * mm, "end": v(-31, -35) * mm});
            skLineSegment(sketch, "E186.MirrorCS", {"start": v(-35, -31) * mm, "end": v(-35, 31) * mm});
            skLineSegment(sketch, "E187.MirrorCS", {"start": v(36, -40) * mm, "end": v(-36, -40) * mm});
            skLineSegment(sketch, "E188.MirrorCS", {"start": v(-40, 36) * mm, "end": v(-40, -36) * mm});
            skPoint(sketch, "E189.MirrorP", {"position": v(40, 40) * mm});
            skPoint(sketch, "E190.MirrorP", {"position": v(35, 35) * mm});
            skPoint(sketch, "E191.MirrorP", {"position": v(35, -35) * mm});
            skArc(sketch, "E192.MirrorCS", {"start": v(1325, 31) * mm, "mid": v(1326.17, 33.83) * mm, "end": v(1329, 35) * mm});
            skArc(sketch, "E193.MirrorCS", {"start": v(1320, 36) * mm, "mid": v(1321.17, 38.83) * mm, "end": v(1324, 40) * mm});
            skArc(sketch, "E194.MirrorCS", {"start": v(-1391, 35) * mm, "mid": v(-1393.83, 33.83) * mm, "end": v(-1395, 31) * mm});
            skArc(sketch, "E195.MirrorCS", {"start": v(-1395, -31) * mm, "mid": v(-1393.83, -33.83) * mm, "end": v(-1391, -35) * mm});
            skPoint(sketch, "E196.MirrorP", {"position": v(40, -40) * mm});
            skArc(sketch, "E197.MirrorCS", {"start": v(1324, -40) * mm, "mid": v(1321.17, -38.83) * mm, "end": v(1320, -36) * mm});
            skArc(sketch, "E198.MirrorCS", {"start": v(1329, -35) * mm, "mid": v(1326.17, -33.83) * mm, "end": v(1325, -31) * mm});
            skArc(sketch, "E199.MirrorCS", {"start": v(-1396, 40) * mm, "mid": v(-1398.83, 38.83) * mm, "end": v(-1400, 36) * mm});
            skLineSegment(sketch, "E200.MirrorCS", {"start": v(1325, -31) * mm, "end": v(1325, 31) * mm});
            skLineSegment(sketch, "E201.MirrorCS", {"start": v(1391, 35) * mm, "end": v(1329, 35) * mm});
            skLineSegment(sketch, "E202.MirrorCS", {"start": v(1320, 36) * mm, "end": v(1320, -36) * mm});
            skLineSegment(sketch, "E203.MirrorCS", {"start": v(-1400, 36) * mm, "end": v(-1400, -36) * mm});
            skLineSegment(sketch, "E204.MirrorCS", {"start": v(-1395, -31) * mm, "end": v(-1395, 31) * mm});
            skLineSegment(sketch, "E205.MirrorCS", {"start": v(1396, -40) * mm, "end": v(1324, -40) * mm});
            skLineSegment(sketch, "E206.MirrorCS", {"start": v(1396, 40) * mm, "end": v(1324, 40) * mm});
            skPoint(sketch, "E207.MirrorP", {"position": v(-35, -35) * mm});
            skArc(sketch, "E208.MirrorCS", {"start": v(1391, 35) * mm, "mid": v(1393.83, 33.83) * mm, "end": v(1395, 31) * mm});
            skArc(sketch, "E209.MirrorCS", {"start": v(1396, 40) * mm, "mid": v(1398.83, 38.83) * mm, "end": v(1400, 36) * mm});
            skLineSegment(sketch, "E210.MirrorCS", {"start": v(1391, -35) * mm, "end": v(1329, -35) * mm});
            skLineSegment(sketch, "E211.MirrorCS", {"start": v(1400, 36) * mm, "end": v(1400, -36) * mm});
            skPoint(sketch, "E212.MirrorP", {"position": v(0, 35) * mm});
            skArc(sketch, "E213.MirrorCS", {"start": v(-1400, -36) * mm, "mid": v(-1398.83, -38.83) * mm, "end": v(-1396, -40) * mm});
            skLineSegment(sketch, "E214.MirrorCS", {"start": v(1395, -31) * mm, "end": v(1395, 31) * mm});
            skPoint(sketch, "E215.MirrorP", {"position": v(-35, 35) * mm});
            skLineSegment(sketch, "E216.MirrorCS", {"start": v(-1391, -35) * mm, "end": v(-1329, -35) * mm});
            skArc(sketch, "E217.MirrorCS", {"start": v(1395, -31) * mm, "mid": v(1393.83, -33.83) * mm, "end": v(1391, -35) * mm});
            skArc(sketch, "E218.MirrorCS", {"start": v(1400, -36) * mm, "mid": v(1398.83, -38.83) * mm, "end": v(1396, -40) * mm});
            skLineSegment(sketch, "E219.MirrorCS", {"start": v(-1391, 35) * mm, "end": v(-1329, 35) * mm});
            skArc(sketch, "E220.MirrorCS", {"start": v(-1329, -35) * mm, "mid": v(-1326.17, -33.83) * mm, "end": v(-1325, -31) * mm});
            skLineSegment(sketch, "E221.MirrorCS", {"start": v(-1396, 40) * mm, "end": v(-1324, 40) * mm});
            skArc(sketch, "E222.MirrorCS", {"start": v(-1325, 31) * mm, "mid": v(-1326.17, 33.83) * mm, "end": v(-1329, 35) * mm});
            skArc(sketch, "E223.MirrorCS", {"start": v(-1320, 36) * mm, "mid": v(-1321.17, 38.83) * mm, "end": v(-1324, 40) * mm});
            skLineSegment(sketch, "E224.MirrorCS", {"start": v(-1396, -40) * mm, "end": v(-1324, -40) * mm});
            skPoint(sketch, "E225.MirrorP", {"position": v(-40, 40) * mm});
            skLineSegment(sketch, "E226.MirrorCS", {"start": v(-1320, 36) * mm, "end": v(-1320, -36) * mm});
            skPoint(sketch, "E227.MirrorP", {"position": v(-40, -40) * mm});
            skArc(sketch, "E228.MirrorCS", {"start": v(-1324, -40) * mm, "mid": v(-1321.17, -38.83) * mm, "end": v(-1320, -36) * mm});
            skLineSegment(sketch, "E229.MirrorCS", {"start": v(-1325, -31) * mm, "end": v(-1325, 31) * mm});
            skPoint(sketch, "E230.MirrorP", {"position": v(1325, -35) * mm});
            skPoint(sketch, "E231.MirrorP", {"position": v(1325, 35) * mm});
            skPoint(sketch, "E232.MirrorP", {"position": v(1395, -35) * mm});
            skPoint(sketch, "E233.MirrorP", {"position": v(1360, 35) * mm});
            skPoint(sketch, "E234.MirrorP", {"position": v(1395, 35) * mm});
            skPoint(sketch, "E235.MirrorP", {"position": v(1320, 40) * mm});
            skPoint(sketch, "E236.MirrorP", {"position": v(-1325, -35) * mm});
            skPoint(sketch, "E237.MirrorP", {"position": v(-1325, 35) * mm});
            skPoint(sketch, "E238.MirrorP", {"position": v(-1395, -35) * mm});
            skPoint(sketch, "E239.MirrorP", {"position": v(-1400, 40) * mm});
            skPoint(sketch, "E240.MirrorP", {"position": v(1320, -40) * mm});
            skLineSegment(sketch, "E241.MirrorCS", {"start": v(0, -860) * mm, "end": v(0, 184.98) * mm, "construction": true});
            skLineSegment(sketch, "E242.MirrorCS", {"start": v(1005.66, 0) * mm, "end": v(1005.66, -860) * mm, "construction": true});
            skLineSegment(sketch, "E243.MirrorCS", {"start": v(1169.83, 0) * mm, "end": v(841.5, 0) * mm, "construction": true});
            skPoint(sketch, "E244.MirrorP", {"position": v(-1320, 40) * mm});
            skPoint(sketch, "E245.MirrorP", {"position": v(1400, -40) * mm});
            skPoint(sketch, "E246.MirrorP", {"position": v(-1395, 35) * mm});
            skPoint(sketch, "E247.MirrorP", {"position": v(1400, 40) * mm});
            skPoint(sketch, "E248.MirrorP", {"position": v(-1400, -40) * mm});
            skPoint(sketch, "E249.MirrorP", {"position": v(-1320, -40) * mm});
            skLineSegment(sketch, "E250.MirrorCS", {"start": v(-35, 829) * mm, "end": v(-35, 891) * mm});
            skLineSegment(sketch, "E251.MirrorCS", {"start": v(-40, 896) * mm, "end": v(-40, 824) * mm});
            skArc(sketch, "E252.MirrorCS", {"start": v(-35, 891) * mm, "mid": v(-33.83, 893.83) * mm, "end": v(-31, 895) * mm});
            skArc(sketch, "E253.MirrorCS", {"start": v(-31, 825) * mm, "mid": v(-33.83, 826.17) * mm, "end": v(-35, 829) * mm});
            skArc(sketch, "E254.MirrorCS", {"start": v(-36, 900) * mm, "mid": v(-38.83, 898.83) * mm, "end": v(-40, 896) * mm});
            skArc(sketch, "E255.MirrorCS", {"start": v(-40, 824) * mm, "mid": v(-38.83, 821.17) * mm, "end": v(-36, 820) * mm});
            skArc(sketch, "E256.MirrorCS", {"start": v(-40, 896) * mm, "mid": v(-38.83, 898.83) * mm, "end": v(-36, 900) * mm});
            skArc(sketch, "E257.MirrorCS", {"start": v(-31, 895) * mm, "mid": v(-33.83, 893.83) * mm, "end": v(-35, 891) * mm});
            skArc(sketch, "E258.MirrorCS", {"start": v(-36, 820) * mm, "mid": v(-38.83, 821.17) * mm, "end": v(-40, 824) * mm});
            skArc(sketch, "E259.MirrorCS", {"start": v(-35, 829) * mm, "mid": v(-33.83, 826.17) * mm, "end": v(-31, 825) * mm});
            skLineSegment(sketch, "E260.MirrorCS", {"start": v(-31, 825) * mm, "end": v(31, 825) * mm});
            skArc(sketch, "E261.MirrorCS", {"start": v(31, 825) * mm, "mid": v(33.83, 826.17) * mm, "end": v(35, 829) * mm});
            skLineSegment(sketch, "E262.MirrorCS", {"start": v(35, 829) * mm, "end": v(35, 891) * mm});
            skLineSegment(sketch, "E263.MirrorCS", {"start": v(40, 896) * mm, "end": v(40, 824) * mm});
            skArc(sketch, "E264.MirrorCS", {"start": v(40, 824) * mm, "mid": v(38.83, 821.17) * mm, "end": v(36, 820) * mm});
            skLineSegment(sketch, "E265.MirrorCS", {"start": v(-31, 895) * mm, "end": v(31, 895) * mm});
            skLineSegment(sketch, "E266.MirrorCS", {"start": v(-36, 820) * mm, "end": v(36, 820) * mm});
            skLineSegment(sketch, "E267.MirrorCS", {"start": v(31, 825) * mm, "end": v(-31, 825) * mm});
            skArc(sketch, "E268.MirrorCS", {"start": v(31, 895) * mm, "mid": v(33.83, 893.83) * mm, "end": v(35, 891) * mm});
            skArc(sketch, "E269.MirrorCS", {"start": v(35, 829) * mm, "mid": v(33.83, 826.17) * mm, "end": v(31, 825) * mm});
            skArc(sketch, "E270.MirrorCS", {"start": v(36, 820) * mm, "mid": v(38.83, 821.17) * mm, "end": v(40, 824) * mm});
            skLineSegment(sketch, "E271.MirrorCS", {"start": v(31, 895) * mm, "end": v(-31, 895) * mm});
            skLineSegment(sketch, "E272.MirrorCS", {"start": v(36, 820) * mm, "end": v(-36, 820) * mm});
            skArc(sketch, "E273.MirrorCS", {"start": v(35, 891) * mm, "mid": v(33.83, 893.83) * mm, "end": v(31, 895) * mm});
            skLineSegment(sketch, "E274.MirrorCS", {"start": v(-36, 900) * mm, "end": v(36, 900) * mm});
            skArc(sketch, "E275.MirrorCS", {"start": v(36, 900) * mm, "mid": v(38.83, 898.83) * mm, "end": v(40, 896) * mm});
            skLineSegment(sketch, "E276.MirrorCS", {"start": v(36, 900) * mm, "end": v(-36, 900) * mm});
            skArc(sketch, "E277.MirrorCS", {"start": v(40, 896) * mm, "mid": v(38.83, 898.83) * mm, "end": v(36, 900) * mm});
            skPoint(sketch, "E278.MirrorP", {"position": v(-35, 825) * mm});
            skPoint(sketch, "E279.MirrorP", {"position": v(-40, 900) * mm});
            skPoint(sketch, "E280.MirrorP", {"position": v(0, 895) * mm});
            skPoint(sketch, "E281.MirrorP", {"position": v(40, 820) * mm});
            skPoint(sketch, "E282.MirrorP", {"position": v(35, 895) * mm});
            skPoint(sketch, "E283.MirrorP", {"position": v(-40, 820) * mm});
            skPoint(sketch, "E284.MirrorP", {"position": v(40, 900) * mm});
            skPoint(sketch, "E285.MirrorP", {"position": v(35, 825) * mm});
            skPoint(sketch, "E286.MirrorP", {"position": v(-35, 895) * mm});
            skLineSegment(sketch, "E287.MirrorCS", {"start": v(0, 860) * mm, "end": v(0, -184.98) * mm, "construction": true});
            skLineSegment(sketch, "E288.MirrorCS", {"start": v(0, 0) * mm, "end": v(0, 1044.98) * mm, "construction": true});
            skSolve(sketch);
        }
        {
            var Q0;
            Q0 = qSketchRegion(id + "F26", true);
            extrude(context, id + "F27", {"entities" : qUnion([Q0]), "depth" : 780 * mm});
        }
        {
            var Q0;
            Q0=makeQuery(id+"F27.opExtrude","SWEPT_FACE",FACE,{"disambiguationData":[OSD([sQuery(id+"F26.wireOp",EDGE,"E84.MirrorCS")])]});
            var sketch = newSketch(context, id + "F28", { "sketchPlane" : qUnion([Q0])});
            skLineSegment(sketch, "E289.bottom", {"start": v(-1320, -500) * mm, "end": v(-40, -500) * mm});
            skLineSegment(sketch, "E289.top", {"start": v(-1320, -580) * mm, "end": v(-40, -580) * mm});
            skLineSegment(sketch, "E289.left", {"start": v(-1320, -500) * mm, "end": v(-1320, -580) * mm});
            skLineSegment(sketch, "E289.right", {"start": v(-40, -500) * mm, "end": v(-40, -580) * mm});
            skLineSegment(sketch, "E290.bottom", {"start": v(40, -500) * mm, "end": v(1320, -500) * mm});
            skLineSegment(sketch, "E290.top", {"start": v(40, -580) * mm, "end": v(1320, -580) * mm});
            skLineSegment(sketch, "E290.left", {"start": v(40, -500) * mm, "end": v(40, -580) * mm});
            skLineSegment(sketch, "E290.right", {"start": v(1320, -500) * mm, "end": v(1320, -580) * mm});
            skSolve(sketch);
        }
        {
            var Q0;
            Q0 = qSketchRegion(id + "F28", true);
            extrude(context, id + "F29", {"entities" : qUnion([Q0]), "oppositeDirection" : true, "depth" : 80 * mm});
        }
        {
            var Q0;
            Q0=makeQuery(id+"F29.opExtrude","SWEPT_FACE",FACE,{"disambiguationData":[OSD([sQuery(id+"F28.wireOp",EDGE,"E290.right")])]});
            var sketch = newSketch(context, id + "F30", { "sketchPlane" : qUnion([Q0])});
            skLineSegment(sketch, "E291.bottom", {"start": v(-891, -505) * mm, "end": v(-829, -505) * mm});
            skLineSegment(sketch, "E291.top", {"start": v(-891, -575) * mm, "end": v(-829, -575) * mm});
            skLineSegment(sketch, "E291.left", {"start": v(-895, -509) * mm, "end": v(-895, -571) * mm});
            skLineSegment(sketch, "E291.right", {"start": v(-825, -509) * mm, "end": v(-825, -571) * mm});
            skPoint(sketch, "E292.visualSharp", {"position": v(-895, -505) * mm});
            skArc(sketch, "E292.filletArc", {"start": v(-891, -505) * mm, "mid": v(-893.83, -506.17) * mm, "end": v(-895, -509) * mm});
            skPoint(sketch, "E293.visualSharp", {"position": v(-825, -505) * mm});
            skArc(sketch, "E293.filletArc", {"start": v(-825, -509) * mm, "mid": v(-826.17, -506.17) * mm, "end": v(-829, -505) * mm});
            skPoint(sketch, "E294.visualSharp", {"position": v(-825, -575) * mm});
            skArc(sketch, "E294.filletArc", {"start": v(-829, -575) * mm, "mid": v(-826.17, -573.83) * mm, "end": v(-825, -571) * mm});
            skPoint(sketch, "E295.visualSharp", {"position": v(-895, -575) * mm});
            skArc(sketch, "E295.filletArc", {"start": v(-895, -571) * mm, "mid": v(-893.83, -573.83) * mm, "end": v(-891, -575) * mm});
            skSolve(sketch);
        }
        {
            var Q0;
            Q0 = qSketchRegion(id + "F30", true);
            extrude(context, id + "F31", {"entities" : qUnion([Q0]), "operationType" : NewBodyOperationType.REMOVE, "oppositeDirection" : true, "depth" : 1280 * mm});
        }
        {
            var Q0;
            Q0=makeQuery(id+"F29.opExtrude","CAP_EDGE",EDGE,{"disambiguationData":[OSD([sQuery(id+"F28.wireOp",EDGE,"E290.bottom")])],"isStart":true});
            var Q1;
            Q1=makeQuery(id+"F29.opExtrude","CAP_EDGE",EDGE,{"disambiguationData":[OSD([sQuery(id+"F28.wireOp",EDGE,"E290.top")])],"isStart":true});
            var Q2;
            Q2=makeQuery(id+"F29.opExtrude","CAP_EDGE",EDGE,{"disambiguationData":[OSD([sQuery(id+"F28.wireOp",EDGE,"E290.bottom")])],"isStart":false});
            var Q3;
            Q3=makeQuery(id+"F29.opExtrude","CAP_EDGE",EDGE,{"disambiguationData":[OSD([sQuery(id+"F28.wireOp",EDGE,"E290.top")])],"isStart":false});
            fillet(context, id + "F32", {"entities" : qUnion([Q0, Q1, Q2, Q3]), "radius" : 4 * mm, "tangentPropagation" : true, "allowEdgeOverflow" : false});
        }
        {
            var Q0;
            Q0=makeQuery(id+"F29.opExtrude","SWEPT_FACE",FACE,{"disambiguationData":[OSD([sQuery(id+"F28.wireOp",EDGE,"E289.right")])]});
            var sketch = newSketch(context, id + "F33", { "sketchPlane" : qUnion([Q0])});
            skLineSegment(sketch, "E296.bottom", {"start": v(-891, -505) * mm, "end": v(-829, -505) * mm});
            skLineSegment(sketch, "E296.top", {"start": v(-891, -575) * mm, "end": v(-829, -575) * mm});
            skLineSegment(sketch, "E296.left", {"start": v(-895, -509) * mm, "end": v(-895, -571) * mm});
            skLineSegment(sketch, "E296.right", {"start": v(-825, -509) * mm, "end": v(-825, -571) * mm});
            skPoint(sketch, "E297.visualSharp", {"position": v(-825, -505) * mm});
            skArc(sketch, "E297.filletArc", {"start": v(-825, -509) * mm, "mid": v(-826.17, -506.17) * mm, "end": v(-829, -505) * mm});
            skPoint(sketch, "E298.visualSharp", {"position": v(-895, -505) * mm});
            skArc(sketch, "E298.filletArc", {"start": v(-891, -505) * mm, "mid": v(-893.83, -506.17) * mm, "end": v(-895, -509) * mm});
            skPoint(sketch, "E299.visualSharp", {"position": v(-895, -575) * mm});
            skArc(sketch, "E299.filletArc", {"start": v(-895, -571) * mm, "mid": v(-893.83, -573.83) * mm, "end": v(-891, -575) * mm});
            skPoint(sketch, "E300.visualSharp", {"position": v(-825, -575) * mm});
            skArc(sketch, "E300.filletArc", {"start": v(-829, -575) * mm, "mid": v(-826.17, -573.83) * mm, "end": v(-825, -571) * mm});
            skSolve(sketch);
        }
        {
            var Q0;
            Q0=makeQuery(id+"F33.imprint","IMPRINT",FACE,{"disambiguationData":[TD([[makeQuery(id+"F33.imprint","IMPRINT",EDGE,{"derivedFrom":sQuery(id+"F33.wireOp",EDGE,"E296.bottom")}),-1.0]])]});
            extrude(context, id + "F34", {"entities" : qUnion([Q0]), "operationType" : NewBodyOperationType.REMOVE, "oppositeDirection" : true, "depth" : 1280 * mm});
        }
        {
            var Q0;
            Q0=makeQuery(id+"F29.opExtrude","CAP_EDGE",EDGE,{"disambiguationData":[OSD([sQuery(id+"F28.wireOp",EDGE,"E289.bottom")])],"isStart":true});
            var Q1;
            Q1=makeQuery(id+"F29.opExtrude","CAP_EDGE",EDGE,{"disambiguationData":[OSD([sQuery(id+"F28.wireOp",EDGE,"E289.bottom")])],"isStart":false});
            var Q2;
            Q2=makeQuery(id+"F29.opExtrude","CAP_EDGE",EDGE,{"disambiguationData":[OSD([sQuery(id+"F28.wireOp",EDGE,"E289.top")])],"isStart":true});
            var Q3;
            Q3=makeQuery(id+"F29.opExtrude","CAP_EDGE",EDGE,{"disambiguationData":[OSD([sQuery(id+"F28.wireOp",EDGE,"E289.top")])],"isStart":false});
            fillet(context, id + "F35", {"entities" : qUnion([Q0, Q1, Q2, Q3]), "radius" : 4 * mm, "tangentPropagation" : true, "allowEdgeOverflow" : false});
        }
        {
            var Q0;
            Q0=makeQuery(id+"F27.opExtrude","SWEPT_FACE",FACE,{"disambiguationData":[OSD([sQuery(id+"F26.wireOp",EDGE,"E221.MirrorCS")])]});
            var sketch = newSketch(context, id + "F36", { "sketchPlane" : qUnion([Q0])});
            skLineSegment(sketch, "E301.bottom", {"start": v(-1320, -500) * mm, "end": v(-40, -500) * mm});
            skLineSegment(sketch, "E301.top", {"start": v(-1320, -580) * mm, "end": v(-40, -580) * mm});
            skLineSegment(sketch, "E301.left", {"start": v(-1320, -500) * mm, "end": v(-1320, -580) * mm});
            skLineSegment(sketch, "E301.right", {"start": v(-40, -500) * mm, "end": v(-40, -580) * mm});
            skLineSegment(sketch, "E302.bottom", {"start": v(40, -500) * mm, "end": v(1320, -500) * mm});
            skLineSegment(sketch, "E302.top", {"start": v(40, -580) * mm, "end": v(1320, -580) * mm});
            skLineSegment(sketch, "E302.left", {"start": v(40, -500) * mm, "end": v(40, -580) * mm});
            skLineSegment(sketch, "E302.right", {"start": v(1320, -500) * mm, "end": v(1320, -580) * mm});
            skSolve(sketch);
        }
        {
            var Q0;
            Q0=makeQuery(id+"F36.imprint","IMPRINT",FACE,{"disambiguationData":[TD([[makeQuery(id+"F36.imprint","IMPRINT",EDGE,{"derivedFrom":sQuery(id+"F36.wireOp",EDGE,"E301.bottom")}),-1.0]])]});
            var Q1;
            Q1=makeQuery(id+"F36.imprint","IMPRINT",FACE,{"disambiguationData":[TD([[makeQuery(id+"F36.imprint","IMPRINT",EDGE,{"derivedFrom":sQuery(id+"F36.wireOp",EDGE,"E302.bottom")}),-1.0]])]});
            extrude(context, id + "F37", {"entities" : qUnion([Q0, Q1]), "oppositeDirection" : true, "depth" : 80 * mm});
        }
        {
            var Q0;
            Q0=makeQuery(id+"F27.opExtrude","SWEPT_FACE",FACE,{"disambiguationData":[OSD([sQuery(id+"F26.wireOp",EDGE,"E33.bottom")])]});
            var sketch = newSketch(context, id + "F38", { "sketchPlane" : qUnion([Q0])});
            skLineSegment(sketch, "E303.bottom", {"start": v(-1320, -500) * mm, "end": v(-40, -500) * mm});
            skLineSegment(sketch, "E303.top", {"start": v(-1320, -580) * mm, "end": v(-40, -580) * mm});
            skLineSegment(sketch, "E303.left", {"start": v(-1320, -500) * mm, "end": v(-1320, -580) * mm});
            skLineSegment(sketch, "E303.right", {"start": v(-40, -500) * mm, "end": v(-40, -580) * mm});
            skLineSegment(sketch, "E304.bottom", {"start": v(40, -500) * mm, "end": v(1320, -500) * mm});
            skLineSegment(sketch, "E304.top", {"start": v(40, -580) * mm, "end": v(1320, -580) * mm});
            skLineSegment(sketch, "E304.left", {"start": v(40, -500) * mm, "end": v(40, -580) * mm});
            skLineSegment(sketch, "E304.right", {"start": v(1320, -500) * mm, "end": v(1320, -580) * mm});
            skSolve(sketch);
        }
        {
            var Q0;
            Q0 = qSketchRegion(id + "F38", true);
            extrude(context, id + "F39", {"entities" : qUnion([Q0]), "oppositeDirection" : true, "depth" : 80 * mm});
        }
        {
            var Q0;
            Q0=makeQuery(id+"F37.opExtrude","SWEPT_FACE",FACE,{"disambiguationData":[OSD([sQuery(id+"F36.wireOp",EDGE,"E302.right")])]});
            var sketch = newSketch(context, id + "F40", { "sketchPlane" : qUnion([Q0])});
            skLineSegment(sketch, "E305.bottom", {"start": v(-31, -505) * mm, "end": v(31, -505) * mm});
            skLineSegment(sketch, "E305.top", {"start": v(-31, -575) * mm, "end": v(31, -575) * mm});
            skLineSegment(sketch, "E305.left", {"start": v(-35, -509) * mm, "end": v(-35, -571) * mm});
            skLineSegment(sketch, "E305.right", {"start": v(35, -509) * mm, "end": v(35, -571) * mm});
            skPoint(sketch, "E306.visualSharp", {"position": v(-35, -505) * mm});
            skArc(sketch, "E306.filletArc", {"start": v(-31, -505) * mm, "mid": v(-33.83, -506.17) * mm, "end": v(-35, -509) * mm});
            skPoint(sketch, "E307.visualSharp", {"position": v(35, -505) * mm});
            skArc(sketch, "E307.filletArc", {"start": v(35, -509) * mm, "mid": v(33.83, -506.17) * mm, "end": v(31, -505) * mm});
            skPoint(sketch, "E308.visualSharp", {"position": v(-35, -575) * mm});
            skArc(sketch, "E308.filletArc", {"start": v(-35, -571) * mm, "mid": v(-33.83, -573.83) * mm, "end": v(-31, -575) * mm});
            skPoint(sketch, "E309.visualSharp", {"position": v(35, -575) * mm});
            skArc(sketch, "E309.filletArc", {"start": v(31, -575) * mm, "mid": v(33.83, -573.83) * mm, "end": v(35, -571) * mm});
            skLineSegment(sketch, "E310.bottom", {"start": v(829, -505) * mm, "end": v(891, -505) * mm});
            skLineSegment(sketch, "E310.top", {"start": v(829, -575) * mm, "end": v(891, -575) * mm});
            skLineSegment(sketch, "E310.left", {"start": v(825, -509) * mm, "end": v(825, -571) * mm});
            skLineSegment(sketch, "E310.right", {"start": v(895, -509) * mm, "end": v(895, -571) * mm});
            skPoint(sketch, "E311.visualSharp", {"position": v(825, -505) * mm});
            skArc(sketch, "E311.filletArc", {"start": v(829, -505) * mm, "mid": v(826.17, -506.17) * mm, "end": v(825, -509) * mm});
            skPoint(sketch, "E312.visualSharp", {"position": v(895, -505) * mm});
            skArc(sketch, "E312.filletArc", {"start": v(895, -509) * mm, "mid": v(893.83, -506.17) * mm, "end": v(891, -505) * mm});
            skPoint(sketch, "E313.visualSharp", {"position": v(895, -575) * mm});
            skArc(sketch, "E313.filletArc", {"start": v(891, -575) * mm, "mid": v(893.83, -573.83) * mm, "end": v(895, -571) * mm});
            skPoint(sketch, "E314.visualSharp", {"position": v(825, -575) * mm});
            skArc(sketch, "E314.filletArc", {"start": v(825, -571) * mm, "mid": v(826.17, -573.83) * mm, "end": v(829, -575) * mm});
            skSolve(sketch);
        }
        {
            var Q0;
            Q0 = qSketchRegion(id + "F40", true);
            extrude(context, id + "F41", {"entities" : qUnion([Q0]), "operationType" : NewBodyOperationType.REMOVE, "oppositeDirection" : true, "depth" : 1280 * mm});
        }
        {
            var Q0;
            Q0=makeQuery(id+"F37.opExtrude","CAP_EDGE",EDGE,{"disambiguationData":[OSD([sQuery(id+"F36.wireOp",EDGE,"E302.bottom")])],"isStart":true});
            var Q1;
            Q1=makeQuery(id+"F37.opExtrude","CAP_EDGE",EDGE,{"disambiguationData":[OSD([sQuery(id+"F36.wireOp",EDGE,"E302.bottom")])],"isStart":false});
            var Q2;
            Q2=makeQuery(id+"F37.opExtrude","CAP_EDGE",EDGE,{"disambiguationData":[OSD([sQuery(id+"F36.wireOp",EDGE,"E302.top")])],"isStart":true});
            var Q3;
            Q3=makeQuery(id+"F37.opExtrude","CAP_EDGE",EDGE,{"disambiguationData":[OSD([sQuery(id+"F36.wireOp",EDGE,"E302.top")])],"isStart":false});
            var Q4;
            Q4=makeQuery(id+"F39.opExtrude","CAP_EDGE",EDGE,{"disambiguationData":[OSD([sQuery(id+"F38.wireOp",EDGE,"E303.top")])],"isStart":true});
            var Q5;
            Q5=makeQuery(id+"F39.opExtrude","CAP_EDGE",EDGE,{"disambiguationData":[OSD([sQuery(id+"F38.wireOp",EDGE,"E303.bottom")])],"isStart":true});
            var Q6;
            Q6=makeQuery(id+"F39.opExtrude","CAP_EDGE",EDGE,{"disambiguationData":[OSD([sQuery(id+"F38.wireOp",EDGE,"E303.bottom")])],"isStart":false});
            var Q7;
            Q7=makeQuery(id+"F39.opExtrude","CAP_EDGE",EDGE,{"disambiguationData":[OSD([sQuery(id+"F38.wireOp",EDGE,"E303.top")])],"isStart":false});
            fillet(context, id + "F42", {"entities" : qUnion([Q0, Q1, Q2, Q3, Q4, Q5, Q6, Q7]), "radius" : 4 * mm, "tangentPropagation" : true, "allowEdgeOverflow" : false});
        }
        {
            var Q0;
            Q0=makeQuery(id+"F39.opExtrude","SWEPT_FACE",FACE,{"disambiguationData":[OSD([sQuery(id+"F38.wireOp",EDGE,"E304.right")])]});
            var sketch = newSketch(context, id + "F43", { "sketchPlane" : qUnion([Q0])});
            skLineSegment(sketch, "E315.bottom", {"start": v(-891, -505) * mm, "end": v(-829, -505) * mm});
            skLineSegment(sketch, "E315.top", {"start": v(-891, -575) * mm, "end": v(-829, -575) * mm});
            skLineSegment(sketch, "E315.left", {"start": v(-895, -509) * mm, "end": v(-895, -571) * mm});
            skLineSegment(sketch, "E315.right", {"start": v(-825, -509) * mm, "end": v(-825, -571) * mm});
            skPoint(sketch, "E316.visualSharp", {"position": v(-895, -505) * mm});
            skArc(sketch, "E316.filletArc", {"start": v(-891, -505) * mm, "mid": v(-893.83, -506.17) * mm, "end": v(-895, -509) * mm});
            skPoint(sketch, "E317.visualSharp", {"position": v(-825, -505) * mm});
            skArc(sketch, "E317.filletArc", {"start": v(-825, -509) * mm, "mid": v(-826.17, -506.17) * mm, "end": v(-829, -505) * mm});
            skPoint(sketch, "E318.visualSharp", {"position": v(-825, -575) * mm});
            skArc(sketch, "E318.filletArc", {"start": v(-829, -575) * mm, "mid": v(-826.17, -573.83) * mm, "end": v(-825, -571) * mm});
            skPoint(sketch, "E319.visualSharp", {"position": v(-895, -575) * mm});
            skArc(sketch, "E319.filletArc", {"start": v(-895, -571) * mm, "mid": v(-893.83, -573.83) * mm, "end": v(-891, -575) * mm});
            skLineSegment(sketch, "E320.bottom", {"start": v(-31, -505) * mm, "end": v(31, -505) * mm});
            skLineSegment(sketch, "E320.top", {"start": v(-31, -575) * mm, "end": v(31, -575) * mm});
            skLineSegment(sketch, "E320.left", {"start": v(-35, -509) * mm, "end": v(-35, -571) * mm});
            skLineSegment(sketch, "E320.right", {"start": v(35, -509) * mm, "end": v(35, -571) * mm});
            skPoint(sketch, "E321.visualSharp", {"position": v(-35, -505) * mm});
            skArc(sketch, "E321.filletArc", {"start": v(-31, -505) * mm, "mid": v(-33.83, -506.17) * mm, "end": v(-35, -509) * mm});
            skPoint(sketch, "E322.visualSharp", {"position": v(35, -505) * mm});
            skArc(sketch, "E322.filletArc", {"start": v(35, -509) * mm, "mid": v(33.83, -506.17) * mm, "end": v(31, -505) * mm});
            skPoint(sketch, "E323.visualSharp", {"position": v(-35, -575) * mm});
            skArc(sketch, "E323.filletArc", {"start": v(-35, -571) * mm, "mid": v(-33.83, -573.83) * mm, "end": v(-31, -575) * mm});
            skPoint(sketch, "E324.visualSharp", {"position": v(35, -575) * mm});
            skArc(sketch, "E324.filletArc", {"start": v(31, -575) * mm, "mid": v(33.83, -573.83) * mm, "end": v(35, -571) * mm});
            skSolve(sketch);
        }
        {
            var Q0;
            Q0 = qSketchRegion(id + "F43", true);
            extrude(context, id + "F44", {"entities" : qUnion([Q0]), "operationType" : NewBodyOperationType.REMOVE, "oppositeDirection" : true, "depth" : 1280 * mm});
        }
        {
            var Q0;
            Q0=makeQuery(id+"F39.opExtrude","CAP_EDGE",EDGE,{"disambiguationData":[OSD([sQuery(id+"F38.wireOp",EDGE,"E304.bottom")])],"isStart":true});
            var Q1;
            Q1=makeQuery(id+"F39.opExtrude","CAP_EDGE",EDGE,{"disambiguationData":[OSD([sQuery(id+"F38.wireOp",EDGE,"E304.bottom")])],"isStart":false});
            var Q2;
            Q2=makeQuery(id+"F39.opExtrude","CAP_EDGE",EDGE,{"disambiguationData":[OSD([sQuery(id+"F38.wireOp",EDGE,"E304.top")])],"isStart":true});
            var Q3;
            Q3=makeQuery(id+"F39.opExtrude","CAP_EDGE",EDGE,{"disambiguationData":[OSD([sQuery(id+"F38.wireOp",EDGE,"E304.top")])],"isStart":false});
            fillet(context, id + "F45", {"entities" : qUnion([Q0, Q1, Q2, Q3]), "radius" : 4 * mm, "tangentPropagation" : true, "allowEdgeOverflow" : false});
        }
        {
            var Q0;
            Q0=makeQuery(id+"F37.opExtrude","CAP_EDGE",EDGE,{"disambiguationData":[OSD([sQuery(id+"F36.wireOp",EDGE,"E301.bottom")])],"isStart":false});
            var Q1;
            Q1=makeQuery(id+"F37.opExtrude","CAP_EDGE",EDGE,{"disambiguationData":[OSD([sQuery(id+"F36.wireOp",EDGE,"E301.bottom")])],"isStart":true});
            var Q2;
            Q2=makeQuery(id+"F37.opExtrude","CAP_EDGE",EDGE,{"disambiguationData":[OSD([sQuery(id+"F36.wireOp",EDGE,"E301.top")])],"isStart":true});
            var Q3;
            Q3=makeQuery(id+"F37.opExtrude","CAP_EDGE",EDGE,{"disambiguationData":[OSD([sQuery(id+"F36.wireOp",EDGE,"E301.top")])],"isStart":false});
            fillet(context, id + "F46", {"entities" : qUnion([Q0, Q1, Q2, Q3]), "radius" : 4 * mm, "tangentPropagation" : true, "allowEdgeOverflow" : false});
        }
        {
            var Q0;
            Q0=makeQuery(id+"F27.opExtrude","SWEPT_FACE",FACE,{"disambiguationData":[OSD([sQuery(id+"F26.wireOp",EDGE,"E59.MirrorCS")])]});
            var sketch = newSketch(context, id + "F47", { "sketchPlane" : qUnion([Q0])});
            skLineSegment(sketch, "E325.bottom", {"start": v(-820, -500) * mm, "end": v(-40, -500) * mm});
            skLineSegment(sketch, "E325.top", {"start": v(-820, -580) * mm, "end": v(-40, -580) * mm});
            skLineSegment(sketch, "E325.left", {"start": v(-820, -500) * mm, "end": v(-820, -580) * mm});
            skLineSegment(sketch, "E325.right", {"start": v(-40, -500) * mm, "end": v(-40, -580) * mm});
            skLineSegment(sketch, "E326.bottom", {"start": v(40, -500) * mm, "end": v(820, -500) * mm});
            skLineSegment(sketch, "E326.top", {"start": v(40, -580) * mm, "end": v(820, -580) * mm});
            skLineSegment(sketch, "E326.left", {"start": v(40, -500) * mm, "end": v(40, -580) * mm});
            skLineSegment(sketch, "E326.right", {"start": v(820, -500) * mm, "end": v(820, -580) * mm});
            skSolve(sketch);
        }
        {
            var Q0;
            Q0 = qSketchRegion(id + "F47", true);
            extrude(context, id + "F48", {"entities" : qUnion([Q0]), "oppositeDirection" : true, "depth" : 80 * mm});
        }
        {
            var Q0;
            Q0=makeQuery(id+"F27.opExtrude","SWEPT_FACE",FACE,{"disambiguationData":[OSD([sQuery(id+"F26.wireOp",EDGE,"E125.MirrorCS")])]});
            var sketch = newSketch(context, id + "F49", { "sketchPlane" : qUnion([Q0])});
            skLineSegment(sketch, "E327.bottom", {"start": v(-820, -500) * mm, "end": v(-40, -500) * mm});
            skLineSegment(sketch, "E327.top", {"start": v(-820, -580) * mm, "end": v(-40, -580) * mm});
            skLineSegment(sketch, "E327.left", {"start": v(-820, -500) * mm, "end": v(-820, -580) * mm});
            skLineSegment(sketch, "E327.right", {"start": v(-40, -500) * mm, "end": v(-40, -580) * mm});
            skLineSegment(sketch, "E328.bottom", {"start": v(40, -500) * mm, "end": v(820, -500) * mm});
            skLineSegment(sketch, "E328.top", {"start": v(40, -580) * mm, "end": v(820, -580) * mm});
            skLineSegment(sketch, "E328.left", {"start": v(40, -500) * mm, "end": v(40, -580) * mm});
            skLineSegment(sketch, "E328.right", {"start": v(820, -500) * mm, "end": v(820, -580) * mm});
            skSolve(sketch);
        }
        {
            var Q0;
            Q0 = qSketchRegion(id + "F49", true);
            extrude(context, id + "F50", {"entities" : qUnion([Q0]), "oppositeDirection" : true, "depth" : 80 * mm});
        }
        {
            var Q0;
            Q0=makeQuery(id+"F27.opExtrude","SWEPT_FACE",FACE,{"disambiguationData":[OSD([sQuery(id+"F26.wireOp",EDGE,"E97.MirrorCS")])]});
            var sketch = newSketch(context, id + "F51", { "sketchPlane" : qUnion([Q0])});
            skLineSegment(sketch, "E329.bottom", {"start": v(-820, -500) * mm, "end": v(-40, -500) * mm});
            skLineSegment(sketch, "E329.top", {"start": v(-820, -580) * mm, "end": v(-40, -580) * mm});
            skLineSegment(sketch, "E329.left", {"start": v(-820, -500) * mm, "end": v(-820, -580) * mm});
            skLineSegment(sketch, "E329.right", {"start": v(-40, -500) * mm, "end": v(-40, -580) * mm});
            skLineSegment(sketch, "E330.bottom", {"start": v(40, -500) * mm, "end": v(820, -500) * mm});
            skLineSegment(sketch, "E330.top", {"start": v(40, -580) * mm, "end": v(820, -580) * mm});
            skLineSegment(sketch, "E330.left", {"start": v(40, -500) * mm, "end": v(40, -580) * mm});
            skLineSegment(sketch, "E330.right", {"start": v(820, -500) * mm, "end": v(820, -580) * mm});
            skSolve(sketch);
        }
        {
            var Q0;
            Q0 = qSketchRegion(id + "F51", true);
            extrude(context, id + "F52", {"entities" : qUnion([Q0]), "oppositeDirection" : true, "depth" : 80 * mm});
        }
        {
            var Q0;
            Q0=makeQuery(id+"F48.opExtrude","SWEPT_FACE",FACE,{"disambiguationData":[OSD([sQuery(id+"F47.wireOp",EDGE,"E326.right")])]});
            var sketch = newSketch(context, id + "F53", { "sketchPlane" : qUnion([Q0])});
            skLineSegment(sketch, "E331.bottom", {"start": v(-1391, -505) * mm, "end": v(-1329, -505) * mm});
            skLineSegment(sketch, "E331.top", {"start": v(-1391, -575) * mm, "end": v(-1329, -575) * mm});
            skLineSegment(sketch, "E331.left", {"start": v(-1395, -509) * mm, "end": v(-1395, -571) * mm});
            skLineSegment(sketch, "E331.right", {"start": v(-1325, -509) * mm, "end": v(-1325, -571) * mm});
            skPoint(sketch, "E332.visualSharp", {"position": v(-1395, -505) * mm});
            skArc(sketch, "E332.filletArc", {"start": v(-1391, -505) * mm, "mid": v(-1393.83, -506.17) * mm, "end": v(-1395, -509) * mm});
            skPoint(sketch, "E333.visualSharp", {"position": v(-1325, -505) * mm});
            skArc(sketch, "E333.filletArc", {"start": v(-1325, -509) * mm, "mid": v(-1326.17, -506.17) * mm, "end": v(-1329, -505) * mm});
            skPoint(sketch, "E334.visualSharp", {"position": v(-1325, -575) * mm});
            skArc(sketch, "E334.filletArc", {"start": v(-1329, -575) * mm, "mid": v(-1326.17, -573.83) * mm, "end": v(-1325, -571) * mm});
            skPoint(sketch, "E335.visualSharp", {"position": v(-1395, -575) * mm});
            skArc(sketch, "E335.filletArc", {"start": v(-1395, -571) * mm, "mid": v(-1393.83, -573.83) * mm, "end": v(-1391, -575) * mm});
            skLineSegment(sketch, "E336.bottom", {"start": v(-31, -505) * mm, "end": v(31, -505) * mm});
            skLineSegment(sketch, "E336.top", {"start": v(-31, -575) * mm, "end": v(31, -575) * mm});
            skLineSegment(sketch, "E336.left", {"start": v(-35, -509) * mm, "end": v(-35, -571) * mm});
            skLineSegment(sketch, "E336.right", {"start": v(35, -509) * mm, "end": v(35, -571) * mm});
            skPoint(sketch, "E337.visualSharp", {"position": v(35, -505) * mm});
            skArc(sketch, "E337.filletArc", {"start": v(35, -509) * mm, "mid": v(33.83, -506.17) * mm, "end": v(31, -505) * mm});
            skPoint(sketch, "E338.visualSharp", {"position": v(35, -575) * mm});
            skArc(sketch, "E338.filletArc", {"start": v(31, -575) * mm, "mid": v(33.83, -573.83) * mm, "end": v(35, -571) * mm});
            skPoint(sketch, "E339.visualSharp", {"position": v(-35, -575) * mm});
            skArc(sketch, "E339.filletArc", {"start": v(-35, -571) * mm, "mid": v(-33.83, -573.83) * mm, "end": v(-31, -575) * mm});
            skPoint(sketch, "E340.visualSharp", {"position": v(-35, -505) * mm});
            skArc(sketch, "E340.filletArc", {"start": v(-31, -505) * mm, "mid": v(-33.83, -506.17) * mm, "end": v(-35, -509) * mm});
            skLineSegment(sketch, "E341.bottom", {"start": v(1329, -505) * mm, "end": v(1391, -505) * mm});
            skLineSegment(sketch, "E341.top", {"start": v(1329, -575) * mm, "end": v(1391, -575) * mm});
            skLineSegment(sketch, "E341.left", {"start": v(1325, -509) * mm, "end": v(1325, -571) * mm});
            skLineSegment(sketch, "E341.right", {"start": v(1395, -509) * mm, "end": v(1395, -571) * mm});
            skPoint(sketch, "E342.visualSharp", {"position": v(1325, -505) * mm});
            skArc(sketch, "E342.filletArc", {"start": v(1329, -505) * mm, "mid": v(1326.17, -506.17) * mm, "end": v(1325, -509) * mm});
            skPoint(sketch, "E343.visualSharp", {"position": v(1395, -505) * mm});
            skArc(sketch, "E343.filletArc", {"start": v(1395, -509) * mm, "mid": v(1393.83, -506.17) * mm, "end": v(1391, -505) * mm});
            skPoint(sketch, "E344.visualSharp", {"position": v(1325, -575) * mm});
            skArc(sketch, "E344.filletArc", {"start": v(1325, -571) * mm, "mid": v(1326.17, -573.83) * mm, "end": v(1329, -575) * mm});
            skPoint(sketch, "E345.visualSharp", {"position": v(1395, -575) * mm});
            skArc(sketch, "E345.filletArc", {"start": v(1391, -575) * mm, "mid": v(1393.83, -573.83) * mm, "end": v(1395, -571) * mm});
            skSolve(sketch);
        }
        {
            var Q0;
            Q0 = qSketchRegion(id + "F53", true);
            extrude(context, id + "F54", {"entities" : qUnion([Q0]), "operationType" : NewBodyOperationType.REMOVE, "oppositeDirection" : true, "depth" : 780 * mm});
        }
        {
            var Q0;
            Q0=makeQuery(id+"F48.opExtrude","CAP_EDGE",EDGE,{"disambiguationData":[OSD([sQuery(id+"F47.wireOp",EDGE,"E326.bottom")])],"isStart":true});
            var Q1;
            Q1=makeQuery(id+"F48.opExtrude","CAP_EDGE",EDGE,{"disambiguationData":[OSD([sQuery(id+"F47.wireOp",EDGE,"E326.top")])],"isStart":true});
            var Q2;
            Q2=makeQuery(id+"F48.opExtrude","CAP_EDGE",EDGE,{"disambiguationData":[OSD([sQuery(id+"F47.wireOp",EDGE,"E326.bottom")])],"isStart":false});
            var Q3;
            Q3=makeQuery(id+"F48.opExtrude","CAP_EDGE",EDGE,{"disambiguationData":[OSD([sQuery(id+"F47.wireOp",EDGE,"E326.top")])],"isStart":false});
            var Q4;
            Q4=makeQuery(id+"F50.opExtrude","CAP_EDGE",EDGE,{"disambiguationData":[OSD([sQuery(id+"F49.wireOp",EDGE,"E327.top")])],"isStart":false});
            var Q5;
            Q5=makeQuery(id+"F50.opExtrude","CAP_EDGE",EDGE,{"disambiguationData":[OSD([sQuery(id+"F49.wireOp",EDGE,"E327.top")])],"isStart":true});
            var Q6;
            Q6=makeQuery(id+"F50.opExtrude","CAP_EDGE",EDGE,{"disambiguationData":[OSD([sQuery(id+"F49.wireOp",EDGE,"E327.bottom")])],"isStart":true});
            var Q7;
            Q7=makeQuery(id+"F52.opExtrude","CAP_EDGE",EDGE,{"disambiguationData":[OSD([sQuery(id+"F51.wireOp",EDGE,"E329.bottom")])],"isStart":true});
            var Q8;
            Q8=makeQuery(id+"F52.opExtrude","CAP_EDGE",EDGE,{"disambiguationData":[OSD([sQuery(id+"F51.wireOp",EDGE,"E329.top")])],"isStart":true});
            var Q9;
            Q9=makeQuery(id+"F52.opExtrude","CAP_EDGE",EDGE,{"disambiguationData":[OSD([sQuery(id+"F51.wireOp",EDGE,"E329.top")])],"isStart":false});
            var Q10;
            Q10=makeQuery(id+"F52.opExtrude","CAP_EDGE",EDGE,{"disambiguationData":[OSD([sQuery(id+"F51.wireOp",EDGE,"E329.bottom")])],"isStart":false});
            var Q11;
            Q11=makeQuery(id+"F50.opExtrude","CAP_EDGE",EDGE,{"disambiguationData":[OSD([sQuery(id+"F49.wireOp",EDGE,"E327.bottom")])],"isStart":false});
            fillet(context, id + "F55", {"entities" : qUnion([Q0, Q1, Q2, Q3, Q4, Q5, Q6, Q7, Q8, Q9, Q10, Q11]), "radius" : 4 * mm, "tangentPropagation" : true, "allowEdgeOverflow" : false});
        }
        {
            var Q0;
            Q0=makeQuery(id+"F52.opExtrude","SWEPT_FACE",FACE,{"disambiguationData":[OSD([sQuery(id+"F51.wireOp",EDGE,"E330.right")])]});
            var sketch = newSketch(context, id + "F56", { "sketchPlane" : qUnion([Q0])});
            skLineSegment(sketch, "E346.bottom", {"start": v(-1391, -505) * mm, "end": v(-1329, -505) * mm});
            skLineSegment(sketch, "E346.top", {"start": v(-1391, -575) * mm, "end": v(-1329, -575) * mm});
            skLineSegment(sketch, "E346.left", {"start": v(-1395, -509) * mm, "end": v(-1395, -571) * mm});
            skLineSegment(sketch, "E346.right", {"start": v(-1325, -509) * mm, "end": v(-1325, -571) * mm});
            skPoint(sketch, "E347.visualSharp", {"position": v(-1395, -505) * mm});
            skArc(sketch, "E347.filletArc", {"start": v(-1391, -505) * mm, "mid": v(-1393.83, -506.17) * mm, "end": v(-1395, -509) * mm});
            skPoint(sketch, "E348.visualSharp", {"position": v(-1325, -505) * mm});
            skArc(sketch, "E348.filletArc", {"start": v(-1325, -509) * mm, "mid": v(-1326.17, -506.17) * mm, "end": v(-1329, -505) * mm});
            skPoint(sketch, "E349.visualSharp", {"position": v(-1325, -575) * mm});
            skArc(sketch, "E349.filletArc", {"start": v(-1329, -575) * mm, "mid": v(-1326.17, -573.83) * mm, "end": v(-1325, -571) * mm});
            skPoint(sketch, "E350.visualSharp", {"position": v(-1395, -575) * mm});
            skArc(sketch, "E350.filletArc", {"start": v(-1395, -571) * mm, "mid": v(-1393.83, -573.83) * mm, "end": v(-1391, -575) * mm});
            skLineSegment(sketch, "E351.bottom", {"start": v(-31, -505) * mm, "end": v(31, -505) * mm});
            skLineSegment(sketch, "E351.top", {"start": v(-31, -575) * mm, "end": v(31, -575) * mm});
            skLineSegment(sketch, "E351.left", {"start": v(-35, -509) * mm, "end": v(-35, -571) * mm});
            skLineSegment(sketch, "E351.right", {"start": v(35, -509) * mm, "end": v(35, -571) * mm});
            skPoint(sketch, "E352.visualSharp", {"position": v(-35, -505) * mm});
            skArc(sketch, "E352.filletArc", {"start": v(-31, -505) * mm, "mid": v(-33.83, -506.17) * mm, "end": v(-35, -509) * mm});
            skPoint(sketch, "E353.visualSharp", {"position": v(35, -505) * mm});
            skArc(sketch, "E353.filletArc", {"start": v(35, -509) * mm, "mid": v(33.83, -506.17) * mm, "end": v(31, -505) * mm});
            skPoint(sketch, "E354.visualSharp", {"position": v(35, -575) * mm});
            skArc(sketch, "E354.filletArc", {"start": v(31, -575) * mm, "mid": v(33.83, -573.83) * mm, "end": v(35, -571) * mm});
            skPoint(sketch, "E355.visualSharp", {"position": v(-35, -575) * mm});
            skArc(sketch, "E355.filletArc", {"start": v(-35, -571) * mm, "mid": v(-33.83, -573.83) * mm, "end": v(-31, -575) * mm});
            skLineSegment(sketch, "E356.bottom", {"start": v(1329, -505) * mm, "end": v(1391, -505) * mm});
            skLineSegment(sketch, "E356.top", {"start": v(1329, -575) * mm, "end": v(1391, -575) * mm});
            skLineSegment(sketch, "E356.left", {"start": v(1325, -509) * mm, "end": v(1325, -571) * mm});
            skLineSegment(sketch, "E356.right", {"start": v(1395, -509) * mm, "end": v(1395, -571) * mm});
            skPoint(sketch, "E357.visualSharp", {"position": v(1325, -505) * mm});
            skArc(sketch, "E357.filletArc", {"start": v(1329, -505) * mm, "mid": v(1326.17, -506.17) * mm, "end": v(1325, -509) * mm});
            skPoint(sketch, "E358.visualSharp", {"position": v(1395, -505) * mm});
            skArc(sketch, "E358.filletArc", {"start": v(1395, -509) * mm, "mid": v(1393.83, -506.17) * mm, "end": v(1391, -505) * mm});
            skPoint(sketch, "E359.visualSharp", {"position": v(1395, -575) * mm});
            skArc(sketch, "E359.filletArc", {"start": v(1391, -575) * mm, "mid": v(1393.83, -573.83) * mm, "end": v(1395, -571) * mm});
            skPoint(sketch, "E360.visualSharp", {"position": v(1325, -575) * mm});
            skArc(sketch, "E360.filletArc", {"start": v(1325, -571) * mm, "mid": v(1326.17, -573.83) * mm, "end": v(1329, -575) * mm});
            skSolve(sketch);
        }
        {
            var Q0;
            Q0 = qSketchRegion(id + "F56", true);
            extrude(context, id + "F57", {"entities" : qUnion([Q0]), "operationType" : NewBodyOperationType.REMOVE, "oppositeDirection" : true, "depth" : 780 * mm});
        }
        {
            var Q0;
            Q0=makeQuery(id+"F52.opExtrude","CAP_EDGE",EDGE,{"disambiguationData":[OSD([sQuery(id+"F51.wireOp",EDGE,"E330.top")])],"isStart":true});
            var Q1;
            Q1=makeQuery(id+"F52.opExtrude","CAP_EDGE",EDGE,{"disambiguationData":[OSD([sQuery(id+"F51.wireOp",EDGE,"E330.bottom")])],"isStart":true});
            var Q2;
            Q2=makeQuery(id+"F52.opExtrude","CAP_EDGE",EDGE,{"disambiguationData":[OSD([sQuery(id+"F51.wireOp",EDGE,"E330.bottom")])],"isStart":false});
            var Q3;
            Q3=makeQuery(id+"F52.opExtrude","CAP_EDGE",EDGE,{"disambiguationData":[OSD([sQuery(id+"F51.wireOp",EDGE,"E330.top")])],"isStart":false});
            var Q4;
            Q4=makeQuery(id+"F50.opExtrude","CAP_EDGE",EDGE,{"disambiguationData":[OSD([sQuery(id+"F49.wireOp",EDGE,"E328.top")])],"isStart":false});
            var Q5;
            Q5=makeQuery(id+"F50.opExtrude","CAP_EDGE",EDGE,{"disambiguationData":[OSD([sQuery(id+"F49.wireOp",EDGE,"E328.top")])],"isStart":true});
            var Q6;
            Q6=makeQuery(id+"F48.opExtrude","CAP_EDGE",EDGE,{"disambiguationData":[OSD([sQuery(id+"F47.wireOp",EDGE,"E325.top")])],"isStart":true});
            var Q7;
            Q7=makeQuery(id+"F48.opExtrude","CAP_EDGE",EDGE,{"disambiguationData":[OSD([sQuery(id+"F47.wireOp",EDGE,"E325.top")])],"isStart":false});
            var Q8;
            Q8=makeQuery(id+"F48.opExtrude","CAP_EDGE",EDGE,{"disambiguationData":[OSD([sQuery(id+"F47.wireOp",EDGE,"E325.bottom")])],"isStart":true});
            var Q9;
            Q9=makeQuery(id+"F50.opExtrude","CAP_EDGE",EDGE,{"disambiguationData":[OSD([sQuery(id+"F49.wireOp",EDGE,"E328.bottom")])],"isStart":false});
            var Q10;
            Q10=makeQuery(id+"F48.opExtrude","CAP_EDGE",EDGE,{"disambiguationData":[OSD([sQuery(id+"F47.wireOp",EDGE,"E325.bottom")])],"isStart":false});
            var Q11;
            Q11=makeQuery(id+"F50.opExtrude","CAP_EDGE",EDGE,{"disambiguationData":[OSD([sQuery(id+"F49.wireOp",EDGE,"E328.bottom")])],"isStart":true});
            fillet(context, id + "F58", {"entities" : qUnion([Q0, Q1, Q2, Q3, Q4, Q5, Q6, Q7, Q8, Q9, Q10, Q11]), "radius" : 4 * mm, "tangentPropagation" : true, "allowEdgeOverflow" : false});
        }
        {
            var Q0;
            Q0=makeQuery(id+"F25.opExtrude","SWEPT_BODY",BODY,{"disambiguationData":[OSD([sQuery(id+"F24.wireOp",EDGE,"E32.bottom"),sQuery(id+"F24.wireOp",EDGE,"E32.top"),sQuery(id+"F24.wireOp",EDGE,"E32.left"),sQuery(id+"F24.wireOp",EDGE,"E32.right")])]});
            deleteBodies(context, id + "F59", {"entities" : qUnion([Q0])});
        }
    });
